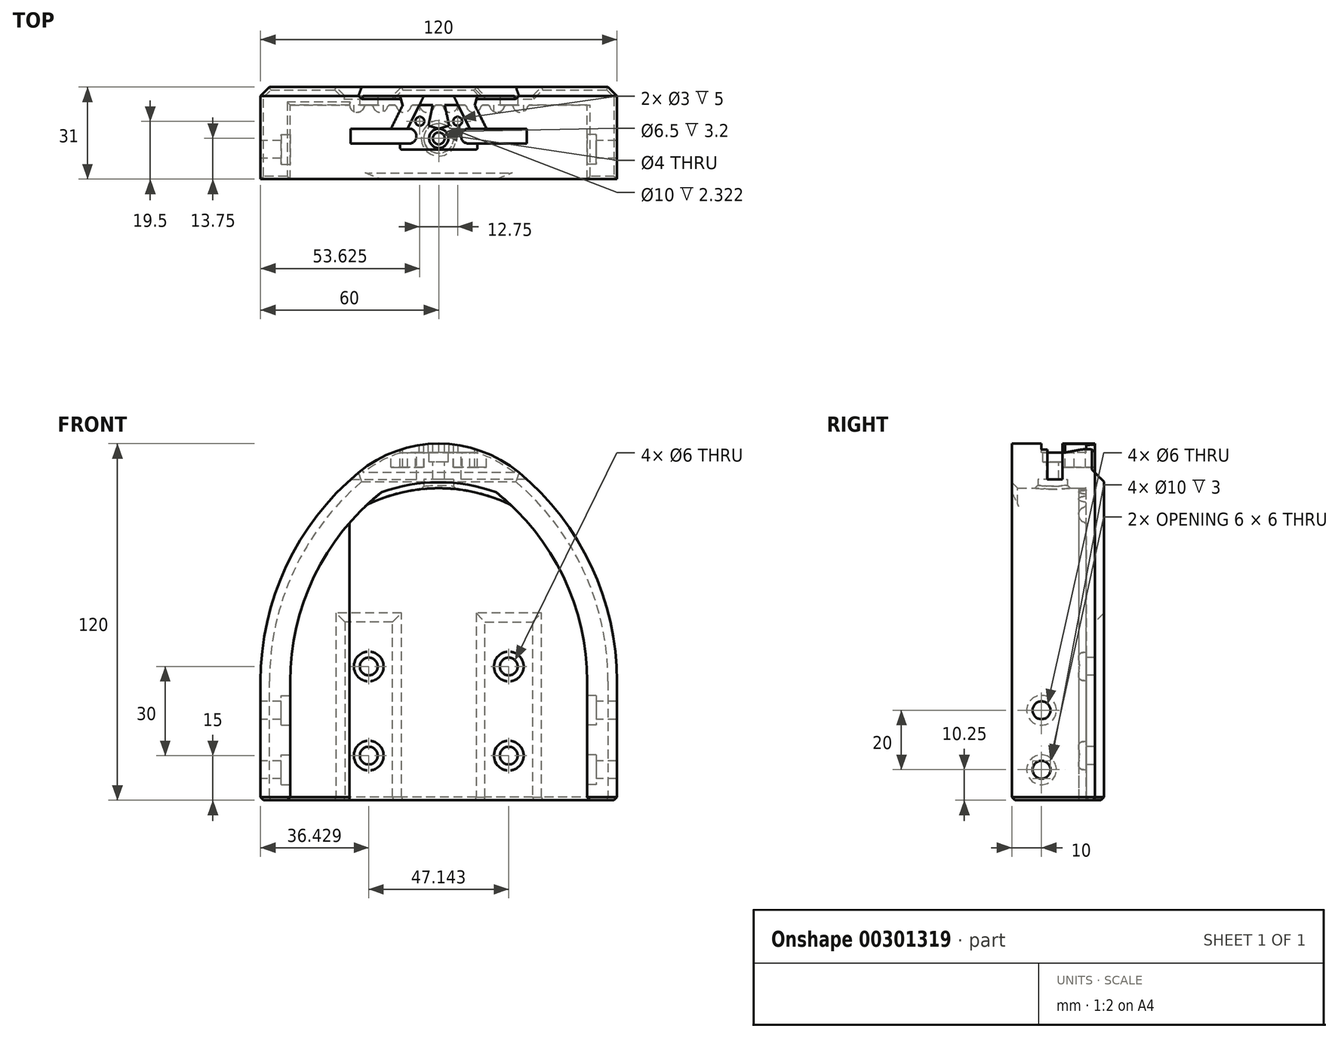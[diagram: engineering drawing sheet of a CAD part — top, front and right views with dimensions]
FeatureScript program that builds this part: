
annotation { "Feature Type Name" : "Feature", "Feature Type Description" : "" }
export const myFeature = defineFeature(function(context is Context, id is Id, definition is map)
    precondition{}
    {
        {
            assignVariable(context, id + "F0", {"name" : "LHeel", "anyValue" : 120 * mm});
        }
        {
            assignVariable(context, id + "F1", {"name" : "THeel", "anyValue" : 15 * mm});
        }
        {
            var Q0;
            Q0=qCreatedBy(makeId("Front.planeOp"),FACE);
            var sketch = newSketch(context, id + "F2", { "sketchPlane" : qUnion([Q0])});
            skArc(sketch, "E0", {"start": v(0, 120) * mm, "mid": v(-14.38, 117.48) * mm, "end": v(-27.05, 110.22) * mm});
            skArc(sketch, "E1", {"start": v(-27.05, 110.22) * mm, "mid": v(-51.35, 78.78) * mm, "end": v(-60, 40) * mm});
            skArc(sketch, "E2.MirrorCS", {"start": v(0, 120) * mm, "mid": v(14.38, 117.48) * mm, "end": v(27.05, 110.22) * mm});
            skArc(sketch, "E3.MirrorCS", {"start": v(27.05, 110.22) * mm, "mid": v(51.35, 78.78) * mm, "end": v(60, 40) * mm});
            skLineSegment(sketch, "E4.top", {"start": v(-60, 0) * mm, "end": v(60, 0) * mm});
            skLineSegment(sketch, "E4.left", {"start": v(-60, 40) * mm, "end": v(-60, 0) * mm});
            skLineSegment(sketch, "E4.right", {"start": v(60, 40) * mm, "end": v(60, 0) * mm});
            skSolve(sketch);
        }
        {
            var Q0;
            Q0=makeQuery(id+"F2.imprint","IMPRINT",FACE,{"disambiguationData":[TD([[makeQuery(id+"F2.imprint","IMPRINT",EDGE,{"derivedFrom":sQuery(id+"F2.wireOp",EDGE,"E0")}),1.0]])]});
            var Q1;
            Q1=makeQuery(id+"F2.imprint","IMPRINT",FACE,{"disambiguationData":[TD([[makeQuery(id+"F2.imprint","IMPRINT",EDGE,{"derivedFrom":sQuery(id+"F2.wireOp",EDGE,"auNxbXKF-pK2V-sqXS-c08M-DIaJRCpJJF02")}),-1.0]])]});
            extrude(context, id + "F3", {"entities" : qUnion([Q0, Q1]), "depth" : 3 * mm});
        }
        {
            var Q0;
            Q0=makeQuery(id+"F3.opExtrude","CAP_FACE",FACE,{"disambiguationData":[OSD([sQuery(id+"F2.wireOp",EDGE,"E0"),sQuery(id+"F2.wireOp",EDGE,"E1"),sQuery(id+"F2.wireOp",EDGE,"auNxbXKF-pK2V-sqXS-c08M-DIaJRCpJJF02"),sQuery(id+"F2.wireOp",EDGE,"E2.MirrorCS"),sQuery(id+"F2.wireOp",EDGE,"E3.MirrorCS"),sQuery(id+"F2.wireOp",EDGE,"bd82aa62-3da5-4588-8fb8-dd676fb609a00.MirrorCS")])],"isStart":false});
            var sketch = newSketch(context, id + "F4", { "sketchPlane" : qUnion([Q0])});
            skArc(sketch, "E5", {"start": v(0, 120) * mm, "mid": v(-14.38, 117.48) * mm, "end": v(-27.05, 110.22) * mm});
            skLineSegment(sketch, "E6", {"start": v(-27.05, 110.22) * mm, "end": v(-27.05, 110.22) * mm});
            skLineSegment(sketch, "E7.MirrorCS", {"start": v(27.05, 110.22) * mm, "end": v(27.05, 110.22) * mm});
            skArc(sketch, "E8.MirrorCS", {"start": v(0, 120) * mm, "mid": v(14.38, 117.48) * mm, "end": v(27.05, 110.22) * mm});
            skArc(sketch, "E9", {"start": v(24.26, 99.36) * mm, "mid": v(0, 105) * mm, "end": v(-24.26, 99.36) * mm});
            skPoint(sketch, "E10", {"position": v(0, 105) * mm});
            skArc(sketch, "E11", {"start": v(60, 40) * mm, "mid": v(51.35, 78.78) * mm, "end": v(27.05, 110.22) * mm});
            skArc(sketch, "E12", {"start": v(-27.05, 110.22) * mm, "mid": v(-51.35, 78.78) * mm, "end": v(-60, 40) * mm});
            skArc(sketch, "E13", {"start": v(-24.26, 99.36) * mm, "mid": v(-43.29, 72.35) * mm, "end": v(-50, 40) * mm});
            skArc(sketch, "E14", {"start": v(50, 40) * mm, "mid": v(43.29, 72.35) * mm, "end": v(24.26, 99.36) * mm});
            skLineSegment(sketch, "E15", {"start": v(-60, 40) * mm, "end": v(-60, 0) * mm});
            skLineSegment(sketch, "E16", {"start": v(-60, 0) * mm, "end": v(-50, 0) * mm});
            skLineSegment(sketch, "E17", {"start": v(-50, 0) * mm, "end": v(-50, 40) * mm});
            skLineSegment(sketch, "E18", {"start": v(50, 40) * mm, "end": v(50, 0) * mm});
            skLineSegment(sketch, "E19", {"start": v(50, 0) * mm, "end": v(60, 0) * mm});
            skLineSegment(sketch, "E20", {"start": v(60, 0) * mm, "end": v(60, 40) * mm});
            skSolve(sketch);
        }
        {
            var Q0;
            Q0=qSketchRegion(id+"F4",true);
            extrude(context, id + "F5", {"entities" : qUnion([Q0]), "operationType" : NewBodyOperationType.ADD, "depth" : 25 * mm});
        }
        {
            var Q0;
            Q0=makeQuery(id+"F5.boolean.opBoolean","MERGE",FACE,{"derivedFrom":[makeQuery(id+"F3.opExtrude","SWEPT_FACE",FACE,{"disambiguationData":[OSD([sQuery(id+"F2.wireOp",EDGE,"E4.top")])]}),makeQuery(id+"F5.opExtrude","SWEPT_FACE",FACE,{"disambiguationData":[OSD([sQuery(id+"F4.wireOp",EDGE,"E16")])]}),makeQuery(id+"F5.opExtrude","SWEPT_FACE",FACE,{"disambiguationData":[OSD([sQuery(id+"F4.wireOp",EDGE,"E19")])]})]});
            var sketch = newSketch(context, id + "F6", { "sketchPlane" : qUnion([Q0])});
            skArc(sketch, "E21", {"start": v(-25, 3) * mm, "mid": v(-27.5, 5.5) * mm, "end": v(-30, 3) * mm});
            skLineSegment(sketch, "E22", {"start": v(-30, 3) * mm, "end": v(-25, 3) * mm});
            skArc(sketch, "E23.1.0.0", {"start": v(-17.14, 3) * mm, "mid": v(-19.64, 5.5) * mm, "end": v(-22.14, 3) * mm});
            skArc(sketch, "E23.2.0.0", {"start": v(-9.29, 3) * mm, "mid": v(-11.79, 5.5) * mm, "end": v(-14.29, 3) * mm});
            skArc(sketch, "E23.3.0.0", {"start": v(-1.43, 3) * mm, "mid": v(-3.93, 5.5) * mm, "end": v(-6.43, 3) * mm});
            skArc(sketch, "E23.4.0.0", {"start": v(6.43, 3) * mm, "mid": v(3.93, 5.5) * mm, "end": v(1.43, 3) * mm});
            skArc(sketch, "E23.5.0.0", {"start": v(14.29, 3) * mm, "mid": v(11.79, 5.5) * mm, "end": v(9.29, 3) * mm});
            skArc(sketch, "E23.6.0.0", {"start": v(22.14, 3) * mm, "mid": v(19.64, 5.5) * mm, "end": v(17.14, 3) * mm});
            skArc(sketch, "E23.7.0.0", {"start": v(30, 3) * mm, "mid": v(27.5, 5.5) * mm, "end": v(25, 3) * mm});
            skLineSegment(sketch, "E23.direction1", {"start": v(-30, 3) * mm, "end": v(-22.14, 3) * mm, "construction": true});
            skSolve(sketch);
        }
        {
            var Q0;
            Q0=qSketchRegion(id+"F6",true);
            var Q1;
            {var subQ0=sQuery(id+"F6.wireOp",EDGE,"E23.1.0.0");Q1=makeQuery(id+"F6.imprint","IMPRINT",FACE,{"disambiguationData":[TD([[makeQuery(id+"F6.imprint","IMPRINT",EDGE,{"derivedFrom":subQ0}),1.0]])]});}
            var Q2;
            {var subQ0=sQuery(id+"F6.wireOp",EDGE,"E23.2.0.0");Q2=makeQuery(id+"F6.imprint","IMPRINT",FACE,{"disambiguationData":[TD([[makeQuery(id+"F6.imprint","IMPRINT",EDGE,{"derivedFrom":subQ0}),1.0]])]});}
            var Q3;
            {var subQ0=sQuery(id+"F6.wireOp",EDGE,"E23.3.0.0");Q3=makeQuery(id+"F6.imprint","IMPRINT",FACE,{"disambiguationData":[TD([[makeQuery(id+"F6.imprint","IMPRINT",EDGE,{"derivedFrom":subQ0}),1.0]])]});}
            var Q4;
            {var subQ0=sQuery(id+"F6.wireOp",EDGE,"E23.4.0.0");Q4=makeQuery(id+"F6.imprint","IMPRINT",FACE,{"disambiguationData":[TD([[makeQuery(id+"F6.imprint","IMPRINT",EDGE,{"derivedFrom":subQ0}),1.0]])]});}
            var Q5;
            {var subQ0=sQuery(id+"F6.wireOp",EDGE,"E23.5.0.0");Q5=makeQuery(id+"F6.imprint","IMPRINT",FACE,{"disambiguationData":[TD([[makeQuery(id+"F6.imprint","IMPRINT",EDGE,{"derivedFrom":subQ0}),1.0]])]});}
            var Q6;
            {var subQ0=sQuery(id+"F6.wireOp",EDGE,"E23.6.0.0");Q6=makeQuery(id+"F6.imprint","IMPRINT",FACE,{"disambiguationData":[TD([[makeQuery(id+"F6.imprint","IMPRINT",EDGE,{"derivedFrom":subQ0}),1.0]])]});}
            var Q7;
            {var subQ0=sQuery(id+"F6.wireOp",EDGE,"E23.7.0.0");Q7=makeQuery(id+"F6.imprint","IMPRINT",FACE,{"disambiguationData":[TD([[makeQuery(id+"F6.imprint","IMPRINT",EDGE,{"derivedFrom":subQ0}),1.0]])]});}
            var Q8;
            {var subQ0=sQuery(id+"F6.wireOp",EDGE,"E23.8.0.0");Q8=makeQuery(id+"F6.imprint","IMPRINT",FACE,{"disambiguationData":[TD([[makeQuery(id+"F6.imprint","IMPRINT",EDGE,{"derivedFrom":subQ0}),1.0]])]});}
            var Q9;
            {var subQ0=sQuery(id+"F6.wireOp",EDGE,"E23.9.0.0");Q9=makeQuery(id+"F6.imprint","IMPRINT",FACE,{"disambiguationData":[TD([[makeQuery(id+"F6.imprint","IMPRINT",EDGE,{"derivedFrom":subQ0}),1.0]])]});}
            extrude(context, id + "F7", {"entities" : qUnion([Q0, Q1, Q2, Q3, Q4, Q5, Q6, Q7, Q8, Q9]), "operationType" : NewBodyOperationType.ADD, "endBound" : BoundingType.UP_TO_NEXT, "oppositeDirection" : true, "depth" : 25 * mm});
        }
        {
            var Q0;
            {var subQ0=sQuery(id+"F6.wireOp",EDGE,"E22");var subQ1=sQuery(id+"F6.wireOp",EDGE,"E21");var subQ2=sQuery(id+"F2.wireOp",EDGE,"bd82aa62-3da5-4588-8fb8-dd676fb609a00.MirrorCS");var subQ3=sQuery(id+"F2.wireOp",EDGE,"auNxbXKF-pK2V-sqXS-c08M-DIaJRCpJJF02");Q0=makeQuery(id+"F7.opExtrude","SWEPT_EDGE",EDGE,{"disambiguationData":[OSD([subQ3,subQ2,subQ1,subQ0]),TDD([makeQuery(id+"F6.imprint","INTERSECT",VERTEX,{"disambiguationData":[OD(0.0)],"derivedFrom":[makeQuery(id+"F3.opExtrude","CAP_EDGE",EDGE,{"disambiguationData":[OSD([subQ3,subQ2])],"isStart":false}),subQ1,subQ0]})])]});}
            var Q1;
            {var subQ0=sQuery(id+"F6.wireOp",EDGE,"E23.1.0.0");var subQ1=sQuery(id+"F2.wireOp",EDGE,"bd82aa62-3da5-4588-8fb8-dd676fb609a00.MirrorCS");var subQ2=sQuery(id+"F2.wireOp",EDGE,"auNxbXKF-pK2V-sqXS-c08M-DIaJRCpJJF02");Q1=makeQuery(id+"F7.opExtrude","SWEPT_EDGE",EDGE,{"disambiguationData":[OSD([subQ2,subQ1,subQ0]),TDD([makeQuery(id+"F6.imprint","INTERSECT",VERTEX,{"disambiguationData":[OD(0.0)],"derivedFrom":[makeQuery(id+"F3.opExtrude","CAP_EDGE",EDGE,{"disambiguationData":[OSD([subQ2,subQ1])],"isStart":false}),subQ0]})])]});}
            var Q2;
            {var subQ0=sQuery(id+"F6.wireOp",EDGE,"E23.2.0.0");var subQ1=sQuery(id+"F2.wireOp",EDGE,"bd82aa62-3da5-4588-8fb8-dd676fb609a00.MirrorCS");var subQ2=sQuery(id+"F2.wireOp",EDGE,"auNxbXKF-pK2V-sqXS-c08M-DIaJRCpJJF02");Q2=makeQuery(id+"F7.opExtrude","SWEPT_EDGE",EDGE,{"disambiguationData":[OSD([subQ2,subQ1,subQ0]),TDD([makeQuery(id+"F6.imprint","INTERSECT",VERTEX,{"disambiguationData":[OD(0.0)],"derivedFrom":[makeQuery(id+"F3.opExtrude","CAP_EDGE",EDGE,{"disambiguationData":[OSD([subQ2,subQ1])],"isStart":false}),subQ0]})])]});}
            var Q3;
            {var subQ0=sQuery(id+"F6.wireOp",EDGE,"E23.3.0.0");var subQ1=sQuery(id+"F2.wireOp",EDGE,"bd82aa62-3da5-4588-8fb8-dd676fb609a00.MirrorCS");var subQ2=sQuery(id+"F2.wireOp",EDGE,"auNxbXKF-pK2V-sqXS-c08M-DIaJRCpJJF02");Q3=makeQuery(id+"F7.opExtrude","SWEPT_EDGE",EDGE,{"disambiguationData":[OSD([subQ2,subQ1,subQ0]),TDD([makeQuery(id+"F6.imprint","INTERSECT",VERTEX,{"disambiguationData":[OD(0.0)],"derivedFrom":[makeQuery(id+"F3.opExtrude","CAP_EDGE",EDGE,{"disambiguationData":[OSD([subQ2,subQ1])],"isStart":false}),subQ0]})])]});}
            var Q4;
            {var subQ0=sQuery(id+"F6.wireOp",EDGE,"E23.4.0.0");var subQ1=sQuery(id+"F2.wireOp",EDGE,"bd82aa62-3da5-4588-8fb8-dd676fb609a00.MirrorCS");var subQ2=sQuery(id+"F2.wireOp",EDGE,"auNxbXKF-pK2V-sqXS-c08M-DIaJRCpJJF02");Q4=makeQuery(id+"F7.opExtrude","SWEPT_EDGE",EDGE,{"disambiguationData":[OSD([subQ2,subQ1,subQ0]),TDD([makeQuery(id+"F6.imprint","INTERSECT",VERTEX,{"disambiguationData":[OD(0.0)],"derivedFrom":[makeQuery(id+"F3.opExtrude","CAP_EDGE",EDGE,{"disambiguationData":[OSD([subQ2,subQ1])],"isStart":false}),subQ0]})])]});}
            var Q5;
            {var subQ0=sQuery(id+"F6.wireOp",EDGE,"E23.5.0.0");var subQ1=sQuery(id+"F2.wireOp",EDGE,"bd82aa62-3da5-4588-8fb8-dd676fb609a00.MirrorCS");var subQ2=sQuery(id+"F2.wireOp",EDGE,"auNxbXKF-pK2V-sqXS-c08M-DIaJRCpJJF02");Q5=makeQuery(id+"F7.opExtrude","SWEPT_EDGE",EDGE,{"disambiguationData":[OSD([subQ2,subQ1,subQ0]),TDD([makeQuery(id+"F6.imprint","INTERSECT",VERTEX,{"disambiguationData":[OD(0.0)],"derivedFrom":[makeQuery(id+"F3.opExtrude","CAP_EDGE",EDGE,{"disambiguationData":[OSD([subQ2,subQ1])],"isStart":false}),subQ0]})])]});}
            var Q6;
            {var subQ0=sQuery(id+"F6.wireOp",EDGE,"E23.6.0.0");var subQ1=sQuery(id+"F2.wireOp",EDGE,"bd82aa62-3da5-4588-8fb8-dd676fb609a00.MirrorCS");var subQ2=sQuery(id+"F2.wireOp",EDGE,"auNxbXKF-pK2V-sqXS-c08M-DIaJRCpJJF02");Q6=makeQuery(id+"F7.opExtrude","SWEPT_EDGE",EDGE,{"disambiguationData":[OSD([subQ2,subQ1,subQ0]),TDD([makeQuery(id+"F6.imprint","INTERSECT",VERTEX,{"disambiguationData":[OD(0.0)],"derivedFrom":[makeQuery(id+"F3.opExtrude","CAP_EDGE",EDGE,{"disambiguationData":[OSD([subQ2,subQ1])],"isStart":false}),subQ0]})])]});}
            var Q7;
            {var subQ0=sQuery(id+"F6.wireOp",EDGE,"E23.7.0.0");var subQ1=sQuery(id+"F2.wireOp",EDGE,"bd82aa62-3da5-4588-8fb8-dd676fb609a00.MirrorCS");var subQ2=sQuery(id+"F2.wireOp",EDGE,"auNxbXKF-pK2V-sqXS-c08M-DIaJRCpJJF02");Q7=makeQuery(id+"F7.opExtrude","SWEPT_EDGE",EDGE,{"disambiguationData":[OSD([subQ2,subQ1,subQ0]),TDD([makeQuery(id+"F6.imprint","INTERSECT",VERTEX,{"disambiguationData":[OD(0.0)],"derivedFrom":[makeQuery(id+"F3.opExtrude","CAP_EDGE",EDGE,{"disambiguationData":[OSD([subQ2,subQ1])],"isStart":false}),subQ0]})])]});}
            var Q8;
            {var subQ0=sQuery(id+"F6.wireOp",EDGE,"E23.8.0.0");var subQ1=sQuery(id+"F2.wireOp",EDGE,"bd82aa62-3da5-4588-8fb8-dd676fb609a00.MirrorCS");var subQ2=sQuery(id+"F2.wireOp",EDGE,"auNxbXKF-pK2V-sqXS-c08M-DIaJRCpJJF02");Q8=makeQuery(id+"F7.opExtrude","SWEPT_EDGE",EDGE,{"disambiguationData":[OSD([subQ2,subQ1,subQ0]),TDD([makeQuery(id+"F6.imprint","INTERSECT",VERTEX,{"disambiguationData":[OD(0.0)],"derivedFrom":[makeQuery(id+"F3.opExtrude","CAP_EDGE",EDGE,{"disambiguationData":[OSD([subQ2,subQ1])],"isStart":false}),subQ0]})])]});}
            var Q9;
            {var subQ0=sQuery(id+"F6.wireOp",EDGE,"E23.9.0.0");var subQ1=sQuery(id+"F2.wireOp",EDGE,"bd82aa62-3da5-4588-8fb8-dd676fb609a00.MirrorCS");var subQ2=sQuery(id+"F2.wireOp",EDGE,"auNxbXKF-pK2V-sqXS-c08M-DIaJRCpJJF02");Q9=makeQuery(id+"F7.opExtrude","SWEPT_EDGE",EDGE,{"disambiguationData":[OSD([subQ2,subQ1,subQ0]),TDD([makeQuery(id+"F6.imprint","INTERSECT",VERTEX,{"disambiguationData":[OD(0.0)],"derivedFrom":[makeQuery(id+"F3.opExtrude","CAP_EDGE",EDGE,{"disambiguationData":[OSD([subQ2,subQ1])],"isStart":false}),subQ0]})])]});}
            var Q10;
            {var subQ0=sQuery(id+"F6.wireOp",EDGE,"E23.9.0.0");var subQ1=sQuery(id+"F2.wireOp",EDGE,"bd82aa62-3da5-4588-8fb8-dd676fb609a00.MirrorCS");var subQ2=sQuery(id+"F2.wireOp",EDGE,"auNxbXKF-pK2V-sqXS-c08M-DIaJRCpJJF02");Q10=makeQuery(id+"F7.opExtrude","SWEPT_EDGE",EDGE,{"disambiguationData":[OSD([subQ2,subQ1,subQ0]),TDD([makeQuery(id+"F6.imprint","INTERSECT",VERTEX,{"disambiguationData":[OD(1.0)],"derivedFrom":[makeQuery(id+"F3.opExtrude","CAP_EDGE",EDGE,{"disambiguationData":[OSD([subQ2,subQ1])],"isStart":false}),subQ0]})])]});}
            var Q11;
            {var subQ0=sQuery(id+"F6.wireOp",EDGE,"E23.8.0.0");var subQ1=sQuery(id+"F2.wireOp",EDGE,"bd82aa62-3da5-4588-8fb8-dd676fb609a00.MirrorCS");var subQ2=sQuery(id+"F2.wireOp",EDGE,"auNxbXKF-pK2V-sqXS-c08M-DIaJRCpJJF02");Q11=makeQuery(id+"F7.opExtrude","SWEPT_EDGE",EDGE,{"disambiguationData":[OSD([subQ2,subQ1,subQ0]),TDD([makeQuery(id+"F6.imprint","INTERSECT",VERTEX,{"disambiguationData":[OD(1.0)],"derivedFrom":[makeQuery(id+"F3.opExtrude","CAP_EDGE",EDGE,{"disambiguationData":[OSD([subQ2,subQ1])],"isStart":false}),subQ0]})])]});}
            var Q12;
            {var subQ0=sQuery(id+"F6.wireOp",EDGE,"E23.7.0.0");var subQ1=sQuery(id+"F2.wireOp",EDGE,"bd82aa62-3da5-4588-8fb8-dd676fb609a00.MirrorCS");var subQ2=sQuery(id+"F2.wireOp",EDGE,"auNxbXKF-pK2V-sqXS-c08M-DIaJRCpJJF02");Q12=makeQuery(id+"F7.opExtrude","SWEPT_EDGE",EDGE,{"disambiguationData":[OSD([subQ2,subQ1,subQ0]),TDD([makeQuery(id+"F6.imprint","INTERSECT",VERTEX,{"disambiguationData":[OD(1.0)],"derivedFrom":[makeQuery(id+"F3.opExtrude","CAP_EDGE",EDGE,{"disambiguationData":[OSD([subQ2,subQ1])],"isStart":false}),subQ0]})])]});}
            var Q13;
            {var subQ0=sQuery(id+"F6.wireOp",EDGE,"E23.6.0.0");var subQ1=sQuery(id+"F2.wireOp",EDGE,"bd82aa62-3da5-4588-8fb8-dd676fb609a00.MirrorCS");var subQ2=sQuery(id+"F2.wireOp",EDGE,"auNxbXKF-pK2V-sqXS-c08M-DIaJRCpJJF02");Q13=makeQuery(id+"F7.opExtrude","SWEPT_EDGE",EDGE,{"disambiguationData":[OSD([subQ2,subQ1,subQ0]),TDD([makeQuery(id+"F6.imprint","INTERSECT",VERTEX,{"disambiguationData":[OD(1.0)],"derivedFrom":[makeQuery(id+"F3.opExtrude","CAP_EDGE",EDGE,{"disambiguationData":[OSD([subQ2,subQ1])],"isStart":false}),subQ0]})])]});}
            var Q14;
            {var subQ0=sQuery(id+"F6.wireOp",EDGE,"E23.5.0.0");var subQ1=sQuery(id+"F2.wireOp",EDGE,"bd82aa62-3da5-4588-8fb8-dd676fb609a00.MirrorCS");var subQ2=sQuery(id+"F2.wireOp",EDGE,"auNxbXKF-pK2V-sqXS-c08M-DIaJRCpJJF02");Q14=makeQuery(id+"F7.opExtrude","SWEPT_EDGE",EDGE,{"disambiguationData":[OSD([subQ2,subQ1,subQ0]),TDD([makeQuery(id+"F6.imprint","INTERSECT",VERTEX,{"disambiguationData":[OD(1.0)],"derivedFrom":[makeQuery(id+"F3.opExtrude","CAP_EDGE",EDGE,{"disambiguationData":[OSD([subQ2,subQ1])],"isStart":false}),subQ0]})])]});}
            var Q15;
            {var subQ0=sQuery(id+"F6.wireOp",EDGE,"E23.4.0.0");var subQ1=sQuery(id+"F2.wireOp",EDGE,"bd82aa62-3da5-4588-8fb8-dd676fb609a00.MirrorCS");var subQ2=sQuery(id+"F2.wireOp",EDGE,"auNxbXKF-pK2V-sqXS-c08M-DIaJRCpJJF02");Q15=makeQuery(id+"F7.opExtrude","SWEPT_EDGE",EDGE,{"disambiguationData":[OSD([subQ2,subQ1,subQ0]),TDD([makeQuery(id+"F6.imprint","INTERSECT",VERTEX,{"disambiguationData":[OD(1.0)],"derivedFrom":[makeQuery(id+"F3.opExtrude","CAP_EDGE",EDGE,{"disambiguationData":[OSD([subQ2,subQ1])],"isStart":false}),subQ0]})])]});}
            var Q16;
            {var subQ0=sQuery(id+"F6.wireOp",EDGE,"E23.3.0.0");var subQ1=sQuery(id+"F2.wireOp",EDGE,"bd82aa62-3da5-4588-8fb8-dd676fb609a00.MirrorCS");var subQ2=sQuery(id+"F2.wireOp",EDGE,"auNxbXKF-pK2V-sqXS-c08M-DIaJRCpJJF02");Q16=makeQuery(id+"F7.opExtrude","SWEPT_EDGE",EDGE,{"disambiguationData":[OSD([subQ2,subQ1,subQ0]),TDD([makeQuery(id+"F6.imprint","INTERSECT",VERTEX,{"disambiguationData":[OD(1.0)],"derivedFrom":[makeQuery(id+"F3.opExtrude","CAP_EDGE",EDGE,{"disambiguationData":[OSD([subQ2,subQ1])],"isStart":false}),subQ0]})])]});}
            var Q17;
            {var subQ0=sQuery(id+"F6.wireOp",EDGE,"E23.2.0.0");var subQ1=sQuery(id+"F2.wireOp",EDGE,"bd82aa62-3da5-4588-8fb8-dd676fb609a00.MirrorCS");var subQ2=sQuery(id+"F2.wireOp",EDGE,"auNxbXKF-pK2V-sqXS-c08M-DIaJRCpJJF02");Q17=makeQuery(id+"F7.opExtrude","SWEPT_EDGE",EDGE,{"disambiguationData":[OSD([subQ2,subQ1,subQ0]),TDD([makeQuery(id+"F6.imprint","INTERSECT",VERTEX,{"disambiguationData":[OD(1.0)],"derivedFrom":[makeQuery(id+"F3.opExtrude","CAP_EDGE",EDGE,{"disambiguationData":[OSD([subQ2,subQ1])],"isStart":false}),subQ0]})])]});}
            var Q18;
            {var subQ0=sQuery(id+"F6.wireOp",EDGE,"E23.1.0.0");var subQ1=sQuery(id+"F2.wireOp",EDGE,"bd82aa62-3da5-4588-8fb8-dd676fb609a00.MirrorCS");var subQ2=sQuery(id+"F2.wireOp",EDGE,"auNxbXKF-pK2V-sqXS-c08M-DIaJRCpJJF02");Q18=makeQuery(id+"F7.opExtrude","SWEPT_EDGE",EDGE,{"disambiguationData":[OSD([subQ2,subQ1,subQ0]),TDD([makeQuery(id+"F6.imprint","INTERSECT",VERTEX,{"disambiguationData":[OD(1.0)],"derivedFrom":[makeQuery(id+"F3.opExtrude","CAP_EDGE",EDGE,{"disambiguationData":[OSD([subQ2,subQ1])],"isStart":false}),subQ0]})])]});}
            var Q19;
            {var subQ0=sQuery(id+"F6.wireOp",EDGE,"E22");var subQ1=sQuery(id+"F6.wireOp",EDGE,"E21");var subQ2=sQuery(id+"F2.wireOp",EDGE,"bd82aa62-3da5-4588-8fb8-dd676fb609a00.MirrorCS");var subQ3=sQuery(id+"F2.wireOp",EDGE,"auNxbXKF-pK2V-sqXS-c08M-DIaJRCpJJF02");Q19=makeQuery(id+"F7.opExtrude","SWEPT_EDGE",EDGE,{"disambiguationData":[OSD([subQ3,subQ2,subQ1,subQ0]),TDD([makeQuery(id+"F6.imprint","INTERSECT",VERTEX,{"disambiguationData":[OD(1.0)],"derivedFrom":[makeQuery(id+"F3.opExtrude","CAP_EDGE",EDGE,{"disambiguationData":[OSD([subQ3,subQ2])],"isStart":false}),subQ1,subQ0]})])]});}
            fillet(context, id + "F8", {"entities" : qUnion([Q0, Q1, Q2, Q3, Q4, Q5, Q6, Q7, Q8, Q9, Q10, Q11, Q12, Q13, Q14, Q15, Q16, Q17, Q18, Q19]), "radius" : 1 * mm, "tangentPropagation" : true, "allowEdgeOverflow" : false});
        }
        {
            var Q0;
            Q0=qCreatedBy(makeId("Top.planeOp"),FACE);
            cPlane(context, id + "F9", {"entities" : qUnion([Q0]), "cplaneType" : CPlaneType.OFFSET, "offset" : getVariable(context, 'LHeel'), "width" : 150 * mm, "height" : 150 * mm});
        }
        {
            var Q0;
            Q0=qCreatedBy(id+"F9.planeOp",FACE);
            var sketch = newSketch(context, id + "F10", { "sketchPlane" : qUnion([Q0])});
            skLineSegment(sketch, "E24", {"start": v(35, -11) * mm, "end": v(10, -11) * mm});
            skLineSegment(sketch, "E25", {"start": v(10, -16) * mm, "end": v(35, -16) * mm});
            skLineSegment(sketch, "E26", {"start": v(35, -16) * mm, "end": v(35, -11) * mm});
            skArc(sketch, "E27", {"start": v(10, -11) * mm, "mid": v(7.5, -13.5) * mm, "end": v(10, -16) * mm});
            skLineSegment(sketch, "E28.MirrorCS", {"start": v(-35, -11) * mm, "end": v(-10, -11) * mm});
            skLineSegment(sketch, "E29.MirrorCS", {"start": v(-35, -16) * mm, "end": v(-35, -11) * mm});
            skLineSegment(sketch, "E30.MirrorCS", {"start": v(-10, -16) * mm, "end": v(-35, -16) * mm});
            skArc(sketch, "E31.MirrorCS", {"start": v(-10, -11) * mm, "mid": v(-7.5, -13.5) * mm, "end": v(-10, -16) * mm});
            skSolve(sketch);
        }
        {
            var Q0;
            Q0=qSketchRegion(id+"F10",true);
            extrude(context, id + "F11", {"entities" : qUnion([Q0]), "operationType" : NewBodyOperationType.REMOVE, "oppositeDirection" : true, "depth" : 12 * mm});
        }
        {
            var Q0;
            Q0=qCreatedBy(id+"F9.planeOp",FACE);
            var sketch = newSketch(context, id + "F12", { "sketchPlane" : qUnion([Q0])});
            skLineSegment(sketch, "E32", {"start": v(-5, 0) * mm, "end": v(-10.5, -11) * mm});
            skLineSegment(sketch, "E33", {"start": v(-10.5, -11) * mm, "end": v(-16.1, -11) * mm});
            skLineSegment(sketch, "E34", {"start": v(-16.1, -11) * mm, "end": v(-12.16, -3.14) * mm});
            skLineSegment(sketch, "E35", {"start": v(-12.16, -3.14) * mm, "end": v(-13, 0) * mm});
            skLineSegment(sketch, "E36", {"start": v(-13, 0) * mm, "end": v(-5, 0) * mm});
            skLineSegment(sketch, "E37.MirrorCS", {"start": v(12.16, -3.14) * mm, "end": v(13, 0) * mm});
            skLineSegment(sketch, "E38.MirrorCS", {"start": v(13, 0) * mm, "end": v(5, 0) * mm});
            skLineSegment(sketch, "E39.MirrorCS", {"start": v(10.5, -11) * mm, "end": v(16.1, -11) * mm});
            skLineSegment(sketch, "E40.MirrorCS", {"start": v(16.1, -11) * mm, "end": v(12.16, -3.14) * mm});
            skLineSegment(sketch, "E41.MirrorCS", {"start": v(5, 0) * mm, "end": v(10.5, -11) * mm});
            skSolve(sketch);
        }
        {
            var Q0;
            Q0=qSketchRegion(id+"F12",true);
            extrude(context, id + "F13", {"entities" : qUnion([Q0]), "operationType" : NewBodyOperationType.REMOVE, "oppositeDirection" : true, "depth" : 8 * mm});
        }
        {
            var Q0;
            Q0=qCreatedBy(id+"F9.planeOp",FACE);
            var sketch = newSketch(context, id + "F14", { "sketchPlane" : qUnion([Q0])});
            skLineSegment(sketch, "E42", {"start": v(-6.5, -3) * mm, "end": v(-2, -3) * mm});
            skLineSegment(sketch, "E43", {"start": v(-2, -3) * mm, "end": v(-3.5, -10) * mm});
            skLineSegment(sketch, "E44", {"start": v(-3.5, -10) * mm, "end": v(0, -11) * mm});
            skLineSegment(sketch, "E45", {"start": v(-6.5, -3) * mm, "end": v(-10.5, -11) * mm});
            skLineSegment(sketch, "E46", {"start": v(-13, -16) * mm, "end": v(-13, -18) * mm});
            skLineSegment(sketch, "E47", {"start": v(-13, -18) * mm, "end": v(0, -18) * mm});
            skLineSegment(sketch, "E48", {"start": v(-13, -16) * mm, "end": v(-10, -16) * mm});
            skLineSegment(sketch, "E49.MirrorCS", {"start": v(6.5, -3) * mm, "end": v(2, -3) * mm});
            skLineSegment(sketch, "E50.MirrorCS", {"start": v(6.5, -3) * mm, "end": v(10.5, -11) * mm});
            skLineSegment(sketch, "E51.MirrorCS", {"start": v(3.5, -10) * mm, "end": v(0, -11) * mm});
            skLineSegment(sketch, "E52.MirrorCS", {"start": v(2, -3) * mm, "end": v(3.5, -10) * mm});
            skLineSegment(sketch, "E53.MirrorCS", {"start": v(13, -16) * mm, "end": v(13, -18) * mm});
            skLineSegment(sketch, "E54.MirrorCS", {"start": v(13, -18) * mm, "end": v(0, -18) * mm});
            skLineSegment(sketch, "E55.MirrorCS", {"start": v(13, -16) * mm, "end": v(10, -16) * mm});
            skLineSegment(sketch, "E56", {"start": v(-10.5, -11) * mm, "end": v(-10, -11) * mm});
            skArc(sketch, "E57", {"start": v(-10, -16) * mm, "mid": v(-7.5, -13.5) * mm, "end": v(-10, -11) * mm});
            skLineSegment(sketch, "E58.MirrorCS", {"start": v(10.5, -11) * mm, "end": v(10, -11) * mm});
            skArc(sketch, "E59.MirrorCS", {"start": v(10, -16) * mm, "mid": v(7.5, -13.5) * mm, "end": v(10, -11) * mm});
            skSolve(sketch);
        }
        {
            var Q0;
            Q0=qSketchRegion(id+"F14",true);
            extrude(context, id + "F15", {"entities" : qUnion([Q0]), "operationType" : NewBodyOperationType.REMOVE, "oppositeDirection" : true, "depth" : 3 * mm});
        }
        {
            var Q0;
            Q0=makeQuery(id+"F15.boolean.opBoolean","COPY",EDGE,{"derivedFrom":makeQuery(id+"F15.opExtrude","SWEPT_EDGE",EDGE,{"disambiguationData":[OSD([sQuery(id+"F14.wireOp",EDGE,"E53.MirrorCS"),sQuery(id+"F14.wireOp",EDGE,"E54.MirrorCS")])]})});
            var Q1;
            Q1=makeQuery(id+"F15.boolean.opBoolean","COPY",EDGE,{"derivedFrom":makeQuery(id+"F15.opExtrude","SWEPT_EDGE",EDGE,{"disambiguationData":[OSD([sQuery(id+"F14.wireOp",EDGE,"E46"),sQuery(id+"F14.wireOp",EDGE,"E47")])]})});
            fillet(context, id + "F16", {"entities" : qUnion([Q0, Q1]), "radius" : .5 * mm, "tangentPropagation" : true, "allowEdgeOverflow" : false});
        }
        {
            var Q0;
            Q0=makeQuery(id+"F15.boolean.opBoolean","COPY",FACE,{"derivedFrom":makeQuery(id+"F15.opExtrude","CAP_FACE",FACE,{"disambiguationData":[OSD([sQuery(id+"F14.wireOp",EDGE,"E42"),sQuery(id+"F14.wireOp",EDGE,"E43"),sQuery(id+"F14.wireOp",EDGE,"E44"),sQuery(id+"F14.wireOp",EDGE,"E45"),sQuery(id+"F14.wireOp",EDGE,"E46"),sQuery(id+"F14.wireOp",EDGE,"E47"),sQuery(id+"F14.wireOp",EDGE,"E48"),sQuery(id+"F14.wireOp",EDGE,"E49.MirrorCS"),sQuery(id+"F14.wireOp",EDGE,"E50.MirrorCS"),sQuery(id+"F14.wireOp",EDGE,"E51.MirrorCS"),sQuery(id+"F14.wireOp",EDGE,"E52.MirrorCS"),sQuery(id+"F14.wireOp",EDGE,"E53.MirrorCS"),sQuery(id+"F14.wireOp",EDGE,"E54.MirrorCS"),sQuery(id+"F14.wireOp",EDGE,"E55.MirrorCS"),sQuery(id+"F14.wireOp",EDGE,"E56"),sQuery(id+"F14.wireOp",EDGE,"E57"),sQuery(id+"F14.wireOp",EDGE,"E58.MirrorCS"),sQuery(id+"F14.wireOp",EDGE,"E59.MirrorCS")])],"isStart":false})});
            var sketch = newSketch(context, id + "F17", { "sketchPlane" : qUnion([Q0])});
            skCircle(sketch, "E60", {"center": v(0, -14.25) * mm, "radius": 3.25 * mm});
            skSolve(sketch);
        }
        {
            var Q0;
            Q0=qSketchRegion(id+"F17",true);
            extrude(context, id + "F18", {"entities" : qUnion([Q0]), "operationType" : NewBodyOperationType.REMOVE, "oppositeDirection" : true, "depth" : 3.2 * mm});
        }
        {
            var Q0;
            Q0=makeQuery(id+"F15.boolean.opBoolean","COPY",FACE,{"derivedFrom":makeQuery(id+"F15.opExtrude","CAP_FACE",FACE,{"disambiguationData":[OSD([sQuery(id+"F14.wireOp",EDGE,"E42"),sQuery(id+"F14.wireOp",EDGE,"E43"),sQuery(id+"F14.wireOp",EDGE,"E44"),sQuery(id+"F14.wireOp",EDGE,"E45"),sQuery(id+"F14.wireOp",EDGE,"E46"),sQuery(id+"F14.wireOp",EDGE,"E47"),sQuery(id+"F14.wireOp",EDGE,"E48"),sQuery(id+"F14.wireOp",EDGE,"E49.MirrorCS"),sQuery(id+"F14.wireOp",EDGE,"E50.MirrorCS"),sQuery(id+"F14.wireOp",EDGE,"E51.MirrorCS"),sQuery(id+"F14.wireOp",EDGE,"E52.MirrorCS"),sQuery(id+"F14.wireOp",EDGE,"E53.MirrorCS"),sQuery(id+"F14.wireOp",EDGE,"E54.MirrorCS"),sQuery(id+"F14.wireOp",EDGE,"E55.MirrorCS"),sQuery(id+"F14.wireOp",EDGE,"E56"),sQuery(id+"F14.wireOp",EDGE,"E57"),sQuery(id+"F14.wireOp",EDGE,"E58.MirrorCS"),sQuery(id+"F14.wireOp",EDGE,"E59.MirrorCS")])],"isStart":false})});
            var sketch = newSketch(context, id + "F19", { "sketchPlane" : qUnion([Q0])});
            skCircle(sketch, "E61", {"center": v(6.38, -8.5) * mm, "radius": 1.5 * mm});
            skCircle(sketch, "E62.MirrorC", {"center": v(-6.38, -8.5) * mm, "radius": 1.5 * mm});
            skSolve(sketch);
        }
        {
            var Q0;
            Q0=qSketchRegion(id+"F19",true);
            extrude(context, id + "F20", {"entities" : qUnion([Q0]), "operationType" : NewBodyOperationType.REMOVE, "oppositeDirection" : true, "depth" : 5 * mm});
        }
        {
            var Q0;
            Q0=makeQuery(id+"F15.boolean.opBoolean","COPY",FACE,{"derivedFrom":makeQuery(id+"F15.opExtrude","CAP_FACE",FACE,{"disambiguationData":[OSD([sQuery(id+"F14.wireOp",EDGE,"E42"),sQuery(id+"F14.wireOp",EDGE,"E43"),sQuery(id+"F14.wireOp",EDGE,"E44"),sQuery(id+"F14.wireOp",EDGE,"E45"),sQuery(id+"F14.wireOp",EDGE,"E46"),sQuery(id+"F14.wireOp",EDGE,"E47"),sQuery(id+"F14.wireOp",EDGE,"E48"),sQuery(id+"F14.wireOp",EDGE,"E49.MirrorCS"),sQuery(id+"F14.wireOp",EDGE,"E50.MirrorCS"),sQuery(id+"F14.wireOp",EDGE,"E51.MirrorCS"),sQuery(id+"F14.wireOp",EDGE,"E52.MirrorCS"),sQuery(id+"F14.wireOp",EDGE,"E53.MirrorCS"),sQuery(id+"F14.wireOp",EDGE,"E54.MirrorCS"),sQuery(id+"F14.wireOp",EDGE,"E55.MirrorCS"),sQuery(id+"F14.wireOp",EDGE,"E56"),sQuery(id+"F14.wireOp",EDGE,"E57"),sQuery(id+"F14.wireOp",EDGE,"E58.MirrorCS"),sQuery(id+"F14.wireOp",EDGE,"E59.MirrorCS")])],"isStart":false})});
            var sketch = newSketch(context, id + "F21", { "sketchPlane" : qUnion([Q0])});
            skCircle(sketch, "E63", {"center": v(0, -14.25) * mm, "radius": 2 * mm});
            skSolve(sketch);
        }
        {
            var Q0;
            Q0=qSketchRegion(id+"F21",true);
            extrude(context, id + "F22", {"entities" : qUnion([Q0]), "operationType" : NewBodyOperationType.REMOVE, "oppositeDirection" : true, "depth" : 25 * mm});
        }
        {
            var Q0;
            Q0=qCreatedBy(makeId("Top.planeOp"),FACE);
            cPlane(context, id + "F23", {"entities" : qUnion([Q0]), "cplaneType" : CPlaneType.OFFSET, "offset" : getVariable(context, 'LHeel') - getVariable(context, 'THeel'), "width" : 150 * mm, "height" : 150 * mm});
        }
        {
            var Q0;
            Q0=qCreatedBy(id+"F23.planeOp",FACE);
            var sketch = newSketch(context, id + "F24", { "sketchPlane" : qUnion([Q0])});
            skCircle(sketch, "E64", {"center": v(0, -14.25) * mm, "radius": 2 * mm});
            skCircle(sketch, "E65", {"center": v(0, -14.25) * mm, "radius": 5 * mm});
            skSolve(sketch);
        }
        {
            var Q0;
            Q0=qSketchRegion(id+"F24",true);
            extrude(context, id + "F25", {"entities" : qUnion([Q0]), "operationType" : NewBodyOperationType.REMOVE, "depth" : 3 * mm, "hasSecondDirection" : true, "secondDirectionOppositeDirection" : true, "secondDirectionDepth" : 25 * mm});
        }
        {
            var Q0;
            {var subQ0=sQuery(id+"F6.wireOp",EDGE,"E23.6.0.0");var subQ1=sQuery(id+"F2.wireOp",EDGE,"bd82aa62-3da5-4588-8fb8-dd676fb609a00.MirrorCS");var subQ2=sQuery(id+"F2.wireOp",EDGE,"auNxbXKF-pK2V-sqXS-c08M-DIaJRCpJJF02");var subQ3=makeQuery(id+"F7.opExtrude","CAP_FACE",FACE,{"disambiguationData":[OSD([subQ2,subQ1,subQ0])],"isStart":true});var subQ4=makeQuery(id+"F7.opExtrude","CAP_FACE",FACE,{"disambiguationData":[OSD([subQ2,subQ1,sQuery(id+"F6.wireOp",EDGE,"E23.4.0.0")])],"isStart":true});var subQ5=makeQuery(id+"F7.opExtrude","CAP_FACE",FACE,{"disambiguationData":[OSD([subQ2,subQ1,sQuery(id+"F6.wireOp",EDGE,"E23.3.0.0")])],"isStart":true});var subQ6=makeQuery(id+"F3.opExtrude","SWEPT_FACE",FACE,{"disambiguationData":[OSD([subQ2,subQ1])]});var subQ7=makeQuery(id+"F7.opExtrude","CAP_FACE",FACE,{"disambiguationData":[OSD([subQ2,subQ1,sQuery(id+"F6.wireOp",EDGE,"E23.2.0.0")])],"isStart":true});var subQ8=makeQuery(id+"F5.opExtrude","SWEPT_FACE",FACE,{"disambiguationData":[OSD([sQuery(id+"F4.wireOp",EDGE,"FZn0JHBI-A9Gq-jUhd-VDxp-ANsdCAXQZEyL"),sQuery(id+"F4.wireOp",EDGE,"94862bb9-d334-4f4f-86bf-2b5ff63ee9990.MirrorCS")])]});var subQ9=sQuery(id+"F6.wireOp",EDGE,"E23.7.0.0");var subQ10=makeQuery(id+"F7.opExtrude","SWEPT_FACE",FACE,{"disambiguationData":[OSD([subQ9])]});var subQ11=makeQuery(id+"F7.opExtrude","CAP_FACE",FACE,{"disambiguationData":[OSD([subQ2,subQ1,sQuery(id+"F6.wireOp",EDGE,"E23.1.0.0")])],"isStart":true});var subQ12=makeQuery(id+"F7.opExtrude","CAP_FACE",FACE,{"disambiguationData":[OSD([subQ2,subQ1,sQuery(id+"F6.wireOp",EDGE,"E23.5.0.0")])],"isStart":true});var subQ13=makeQuery(id+"F7.opExtrude","CAP_FACE",FACE,{"disambiguationData":[OSD([sQuery(id+"F6.wireOp",EDGE,"E21"),sQuery(id+"F6.wireOp",EDGE,"E22")])],"isStart":true});var subQ14=makeQuery(id+"F7.opExtrude","CAP_FACE",FACE,{"disambiguationData":[OSD([subQ2,subQ1,subQ9])],"isStart":true});var subQ15=sQuery(id+"F6.wireOp",EDGE,"E23.8.0.0");var subQ16=makeQuery(id+"F7.opExtrude","SWEPT_FACE",FACE,{"disambiguationData":[OSD([subQ15])]});var subQ17=makeQuery(id+"F7.opExtrude","CAP_FACE",FACE,{"disambiguationData":[OSD([subQ2,subQ1,subQ15])],"isStart":true});var subQ18=sQuery(id+"F6.wireOp",EDGE,"E23.9.0.0");var subQ19=makeQuery(id+"F7.opExtrude","CAP_FACE",FACE,{"disambiguationData":[OSD([subQ2,subQ1,subQ18])],"isStart":true});var subQ20=makeQuery(id+"F3.opExtrude","CAP_FACE",FACE,{"disambiguationData":[OSD([sQuery(id+"F2.wireOp",EDGE,"E0"),sQuery(id+"F2.wireOp",EDGE,"E1"),subQ2,sQuery(id+"F2.wireOp",EDGE,"E2.MirrorCS"),sQuery(id+"F2.wireOp",EDGE,"E3.MirrorCS"),subQ1])],"isStart":false});Q0=makeQuery(id+"FuolT4ABAihHTZn_1.boolean.opBoolean","MERGE",FACE,{"derivedFrom":[makeQuery(id+"F7.boolean.opBoolean","SPLIT",FACE,{"disambiguationData":[TD([subQ6,subQ8,makeQuery(id+"F5.opExtrude","SWEPT_FACE",FACE,{"disambiguationData":[OSD([sQuery(id+"F4.wireOp",EDGE,"0306e720-a4cd-40da-927f-c33b378fc5130.MirrorCS")])]}),subQ13,subQ11,subQ7,subQ5,subQ4,subQ12,subQ3,subQ14,subQ16,subQ17,makeQuery(id+"F7.opExtrude","SWEPT_FACE",FACE,{"disambiguationData":[OSD([subQ18])]}),subQ19])],"derivedFrom":subQ20}),makeQuery(id+"F7.boolean.opBoolean","SPLIT",FACE,{"disambiguationData":[TD([subQ6,subQ8,subQ13,subQ11,subQ7,subQ5,subQ4,subQ12,makeQuery(id+"F7.opExtrude","SWEPT_FACE",FACE,{"disambiguationData":[OSD([subQ0])]}),subQ3,subQ10,subQ14,subQ17,subQ19])],"derivedFrom":subQ20}),makeQuery(id+"F7.boolean.opBoolean","SPLIT",FACE,{"disambiguationData":[TD([subQ6,subQ8,subQ13,subQ11,subQ7,subQ5,subQ4,subQ12,subQ3,subQ10,subQ14,subQ16,subQ17,subQ19])],"derivedFrom":subQ20}),makeQuery(id+"FuolT4ABAihHTZn_1.opExtrude","SWEPT_FACE",FACE,{"disambiguationData":[OSD([sQuery(id+"FIxBE3dgotSAZQS_1.wireOp",EDGE,"DbaOr28i-rK8a-sUH4-Cgqk-jCIZV5dNe7y5.bottom")])]})]});}
            var sketch = newSketch(context, id + "F26", { "sketchPlane" : qUnion([Q0])});
            skCircle(sketch, "E66", {"center": v(-23.57, 45) * mm, "radius": 3 * mm});
            skCircle(sketch, "E67", {"center": v(-23.57, 15) * mm, "radius": 3 * mm});
            skCircle(sketch, "E68.MirrorC", {"center": v(23.57, 45) * mm, "radius": 3 * mm});
            skCircle(sketch, "E69.MirrorC", {"center": v(23.57, 15) * mm, "radius": 3 * mm});
            skPoint(sketch, "E70", {"position": v(-23.57, 0) * mm});
            skPoint(sketch, "E71", {"position": v(23.57, 0) * mm});
            skSolve(sketch);
        }
        {
            var Q0;
            Q0=qSketchRegion(id+"F26",true);
            extrude(context, id + "F27", {"entities" : qUnion([Q0]), "operationType" : NewBodyOperationType.REMOVE, "oppositeDirection" : true, "depth" : 25 * mm});
        }
        {
            var Q0;
            {var subQ0=sQuery(id+"F2.wireOp",EDGE,"bd82aa62-3da5-4588-8fb8-dd676fb609a00.MirrorCS");var subQ1=sQuery(id+"F2.wireOp",EDGE,"auNxbXKF-pK2V-sqXS-c08M-DIaJRCpJJF02");var subQ2=sQuery(id+"F6.wireOp",EDGE,"E21");var subQ3=sQuery(id+"F2.wireOp",EDGE,"E1");Q0=makeQuery(id+"F7.boolean.opBoolean","SPLIT",FACE,{"disambiguationData":[TD([makeQuery(id+"F3.opExtrude","SWEPT_FACE",FACE,{"disambiguationData":[OSD([subQ3])]}),makeQuery(id+"F3.opExtrude","SWEPT_FACE",FACE,{"disambiguationData":[OSD([subQ1,subQ0])]}),makeQuery(id+"F5.opExtrude","SWEPT_FACE",FACE,{"disambiguationData":[OSD([sQuery(id+"F4.wireOp",EDGE,"E6")])]}),makeQuery(id+"F5.opExtrude","SWEPT_FACE",FACE,{"disambiguationData":[OSD([sQuery(id+"F4.wireOp",EDGE,"pZRC63if-MIhk-IA8v-DNlQ-6x2yv20jE8mF")])]}),makeQuery(id+"F5.opExtrude","SWEPT_FACE",FACE,{"disambiguationData":[OSD([sQuery(id+"F4.wireOp",EDGE,"QKiYiqoZ-9ux7-oAIY-G16o-4d6qDwNjxzcn")])]}),makeQuery(id+"F7.opExtrude","SWEPT_FACE",FACE,{"disambiguationData":[OSD([subQ2])]}),makeQuery(id+"F7.opExtrude","CAP_FACE",FACE,{"disambiguationData":[OSD([subQ2,sQuery(id+"F6.wireOp",EDGE,"E22")])],"isStart":true}),makeQuery(id+"F7.opExtrude","CAP_FACE",FACE,{"disambiguationData":[OSD([subQ1,subQ0,sQuery(id+"F6.wireOp",EDGE,"E23.1.0.0")])],"isStart":true}),makeQuery(id+"F7.opExtrude","CAP_FACE",FACE,{"disambiguationData":[OSD([subQ1,subQ0,sQuery(id+"F6.wireOp",EDGE,"E23.2.0.0")])],"isStart":true}),makeQuery(id+"F7.opExtrude","CAP_FACE",FACE,{"disambiguationData":[OSD([subQ1,subQ0,sQuery(id+"F6.wireOp",EDGE,"E23.3.0.0")])],"isStart":true}),makeQuery(id+"F7.opExtrude","CAP_FACE",FACE,{"disambiguationData":[OSD([subQ1,subQ0,sQuery(id+"F6.wireOp",EDGE,"E23.4.0.0")])],"isStart":true}),makeQuery(id+"F7.opExtrude","CAP_FACE",FACE,{"disambiguationData":[OSD([subQ1,subQ0,sQuery(id+"F6.wireOp",EDGE,"E23.5.0.0")])],"isStart":true}),makeQuery(id+"F7.opExtrude","CAP_FACE",FACE,{"disambiguationData":[OSD([subQ1,subQ0,sQuery(id+"F6.wireOp",EDGE,"E23.6.0.0")])],"isStart":true}),makeQuery(id+"F7.opExtrude","CAP_FACE",FACE,{"disambiguationData":[OSD([subQ1,subQ0,sQuery(id+"F6.wireOp",EDGE,"E23.7.0.0")])],"isStart":true}),makeQuery(id+"F7.opExtrude","CAP_FACE",FACE,{"disambiguationData":[OSD([subQ1,subQ0,sQuery(id+"F6.wireOp",EDGE,"E23.8.0.0")])],"isStart":true}),makeQuery(id+"F7.opExtrude","CAP_FACE",FACE,{"disambiguationData":[OSD([subQ1,subQ0,sQuery(id+"F6.wireOp",EDGE,"E23.9.0.0")])],"isStart":true})])],"derivedFrom":makeQuery(id+"F3.opExtrude","CAP_FACE",FACE,{"disambiguationData":[OSD([sQuery(id+"F2.wireOp",EDGE,"E0"),subQ3,subQ1,sQuery(id+"F2.wireOp",EDGE,"E2.MirrorCS"),sQuery(id+"F2.wireOp",EDGE,"E3.MirrorCS"),subQ0])],"isStart":false})});}
            var sketch = newSketch(context, id + "F28", { "sketchPlane" : qUnion([Q0])});
            skCircle(sketch, "E72", {"center": v(23.57, 45) * mm, "radius": 5 * mm});
            skCircle(sketch, "E73", {"center": v(-23.57, 45) * mm, "radius": 5 * mm});
            skCircle(sketch, "E74", {"center": v(-23.57, 15) * mm, "radius": 5 * mm});
            skCircle(sketch, "E75", {"center": v(23.57, 15) * mm, "radius": 5 * mm});
            skSolve(sketch);
        }
        {
            var Q0;
            Q0=qSketchRegion(id+"F28",true);
            extrude(context, id + "F29", {"entities" : qUnion([Q0]), "operationType" : NewBodyOperationType.REMOVE, "depth" : 25 * mm});
        }
        {
            var Q0;
            Q0=makeQuery(id+"F3.opExtrude","CAP_FACE",FACE,{"disambiguationData":[OSD([sQuery(id+"F2.wireOp",EDGE,"E0"),sQuery(id+"F2.wireOp",EDGE,"E1"),sQuery(id+"F2.wireOp",EDGE,"auNxbXKF-pK2V-sqXS-c08M-DIaJRCpJJF02"),sQuery(id+"F2.wireOp",EDGE,"E2.MirrorCS"),sQuery(id+"F2.wireOp",EDGE,"E3.MirrorCS"),sQuery(id+"F2.wireOp",EDGE,"bd82aa62-3da5-4588-8fb8-dd676fb609a00.MirrorCS")])],"isStart":true});
            var sketch = newSketch(context, id + "F30", { "sketchPlane" : qUnion([Q0])});
            skLineSegment(sketch, "E76", {"start": v(27.05, 110.22) * mm, "end": v(27.05, 110.22) * mm});
            skPoint(sketch, "E77", {"position": v(-23.57, 15) * mm});
            skLineSegment(sketch, "E78.MirrorCS", {"start": v(-27.05, 110.22) * mm, "end": v(-27.05, 110.22) * mm});
            skPoint(sketch, "E79.MirrorP", {"position": v(23.57, 15) * mm});
            skLineSegment(sketch, "E80", {"start": v(-15.57, 0) * mm, "end": v(-15.57, 60) * mm});
            skLineSegment(sketch, "E81", {"start": v(-15.57, 60) * mm, "end": v(-31.57, 60) * mm});
            skPoint(sketch, "E82", {"position": v(-23.57, 45) * mm});
            skLineSegment(sketch, "E83.MirrorCS", {"start": v(15.57, 60) * mm, "end": v(31.57, 60) * mm});
            skLineSegment(sketch, "E84.MirrorCS", {"start": v(15.57, 0) * mm, "end": v(15.57, 60) * mm});
            skPoint(sketch, "E85", {"position": v(0, 20) * mm});
            skPoint(sketch, "E86", {"position": v(0, 0) * mm});
            skLineSegment(sketch, "E87", {"start": v(-15.57, 0) * mm, "end": v(15.57, 0) * mm});
            skLineSegment(sketch, "E88", {"start": v(31.57, 60) * mm, "end": v(31.57, 0) * mm});
            skLineSegment(sketch, "E89", {"start": v(31.57, 0) * mm, "end": v(60, 0) * mm});
            skLineSegment(sketch, "E90", {"start": v(-31.57, 60) * mm, "end": v(-31.57, 0) * mm});
            skLineSegment(sketch, "E91", {"start": v(-31.57, 0) * mm, "end": v(-60, 0) * mm});
            skLineSegment(sketch, "E92", {"start": v(-60, 0) * mm, "end": v(-60, 40) * mm});
            skLineSegment(sketch, "E93", {"start": v(60, 0) * mm, "end": v(60, 40) * mm});
            skArc(sketch, "E94", {"start": v(60, 40) * mm, "mid": v(51.35, 78.78) * mm, "end": v(27.05, 110.22) * mm});
            skArc(sketch, "E95", {"start": v(-27.05, 110.22) * mm, "mid": v(-51.35, 78.78) * mm, "end": v(-60, 40) * mm});
            skLineSegment(sketch, "E96", {"start": v(-27.05, 110.22) * mm, "end": v(27.05, 110.22) * mm});
            skSolve(sketch);
        }
        {
            var Q0;
            Q0=qSketchRegion(id+"F30",true);
            extrude(context, id + "F31", {"entities" : qUnion([Q0]), "operationType" : NewBodyOperationType.ADD, "depth" : 3 * mm});
        }
        {
            var Q0;
            Q0=makeQuery(id+"F31.opExtrude","CAP_EDGE",EDGE,{"disambiguationData":[OSD([sQuery(id+"F30.wireOp",EDGE,"E76")])],"isStart":false});
            var Q1;
            Q1=makeQuery(id+"F5.opExtrude","CAP_EDGE",EDGE,{"disambiguationData":[OSD([sQuery(id+"F4.wireOp",EDGE,"E6")])],"isStart":false});
            var Q2;
            Q2=makeQuery(id+"F5.opExtrude","CAP_EDGE",EDGE,{"disambiguationData":[OSD([sQuery(id+"F4.wireOp",EDGE,"pZRC63if-MIhk-IA8v-DNlQ-6x2yv20jE8mF")])],"isStart":false});
            var Q3;
            Q3=makeQuery(id+"F5.opExtrude","CAP_EDGE",EDGE,{"disambiguationData":[OSD([sQuery(id+"F4.wireOp",EDGE,"E9")])],"isStart":false});
            var Q4;
            Q4=makeQuery(id+"F5.opExtrude","CAP_EDGE",EDGE,{"disambiguationData":[OSD([sQuery(id+"F4.wireOp",EDGE,"0306e720-a4cd-40da-927f-c33b378fc5130.MirrorCS")])],"isStart":false});
            var Q5;
            Q5=makeQuery(id+"F31.opExtrude","CAP_EDGE",EDGE,{"disambiguationData":[OSD([sQuery(id+"F30.wireOp",EDGE,"RUufvIO7-uwLe-X8pw-0LNw-kXID3cHw8el4")])],"isStart":false});
            var Q6;
            Q6=makeQuery(id+"F31.opExtrude","CAP_EDGE",EDGE,{"disambiguationData":[OSD([sQuery(id+"F30.wireOp",EDGE,"E78.MirrorCS")])],"isStart":false});
            var Q7;
            Q7=makeQuery(id+"F31.opExtrude","CAP_EDGE",EDGE,{"disambiguationData":[OSD([sQuery(id+"F30.wireOp",EDGE,"u4Of9TWJ-UFXE-Kmm3-mw3i-iHo4bxCqP4ZF")])],"isStart":false});
            var Q8;
            Q8=makeQuery(id+"F31.opExtrude","CAP_EDGE",EDGE,{"disambiguationData":[OSD([sQuery(id+"F30.wireOp",EDGE,"SiEx8vhQ-fxaC-5RrE-m7GO-d7uEWHyiGlIe")])],"isStart":false});
            var Q9;
            Q9=makeQuery(id+"F31.opExtrude","CAP_EDGE",EDGE,{"disambiguationData":[OSD([sQuery(id+"F30.wireOp",EDGE,"ykEuGFcq-UQF4-khE9-OFNr-bY3PkPlk7WNo")])],"isStart":false});
            var Q10;
            Q10=makeQuery(id+"F31.boolean.opBoolean","MERGE",EDGE,{"derivedFrom":[makeQuery(id+"F5.boolean.opBoolean","MERGE",EDGE,{"derivedFrom":[makeQuery(id+"F3.opExtrude","SWEPT_EDGE",EDGE,{"disambiguationData":[OSD([sQuery(id+"F2.wireOp",EDGE,"E3.MirrorCS"),sQuery(id+"F2.wireOp",EDGE,"bd82aa62-3da5-4588-8fb8-dd676fb609a00.MirrorCS")])]}),makeQuery(id+"F5.opExtrude","SWEPT_EDGE",EDGE,{"disambiguationData":[OSD([sQuery(id+"F4.wireOp",EDGE,"094a8055-67e1-4fbe-9fcd-0e3f748caa500.MirrorCS"),sQuery(id+"F4.wireOp",EDGE,"E7.MirrorCS")])]})]}),makeQuery(id+"F31.opExtrude","SWEPT_EDGE",EDGE,{"disambiguationData":[OSD([sQuery(id+"F30.wireOp",EDGE,"E78.MirrorCS"),sQuery(id+"F30.wireOp",EDGE,"ykEuGFcq-UQF4-khE9-OFNr-bY3PkPlk7WNo")])]})]});
            var Q11;
            Q11=makeQuery(id+"F31.boolean.opBoolean","MERGE",EDGE,{"derivedFrom":[makeQuery(id+"F5.boolean.opBoolean","MERGE",EDGE,{"derivedFrom":[makeQuery(id+"F3.opExtrude","SWEPT_EDGE",EDGE,{"disambiguationData":[OSD([sQuery(id+"F2.wireOp",EDGE,"E1"),sQuery(id+"F2.wireOp",EDGE,"auNxbXKF-pK2V-sqXS-c08M-DIaJRCpJJF02")])]}),makeQuery(id+"F5.opExtrude","SWEPT_EDGE",EDGE,{"disambiguationData":[OSD([sQuery(id+"F4.wireOp",EDGE,"E6"),sQuery(id+"F4.wireOp",EDGE,"QKiYiqoZ-9ux7-oAIY-G16o-4d6qDwNjxzcn")])]})]}),makeQuery(id+"F31.opExtrude","SWEPT_EDGE",EDGE,{"disambiguationData":[OSD([sQuery(id+"F30.wireOp",EDGE,"E76"),sQuery(id+"F30.wireOp",EDGE,"u4Of9TWJ-UFXE-Kmm3-mw3i-iHo4bxCqP4ZF")])]})]});
            chamfer(context, id + "F32", {"entities" : qUnion([Q0, Q1, Q2, Q3, Q4, Q5, Q6, Q7, Q8, Q9, Q10, Q11]), "width" : 2 * mm, "tangentPropagation" : true});
        }
        {
            var Q0;
            Q0=makeQuery(id+"F31.opExtrude","CAP_EDGE",EDGE,{"disambiguationData":[OSD([sQuery(id+"F30.wireOp",EDGE,"9e28845e-500e-4894-8802-eb7ad12137a14.MirrorCS")])],"isStart":false});
            var Q1;
            Q1=makeQuery(id+"F31.opExtrude","CAP_EDGE",EDGE,{"disambiguationData":[OSD([sQuery(id+"F30.wireOp",EDGE,"E83.MirrorCS")])],"isStart":false});
            var Q2;
            Q2=makeQuery(id+"F31.opExtrude","CAP_EDGE",EDGE,{"disambiguationData":[OSD([sQuery(id+"F30.wireOp",EDGE,"E84.MirrorCS")])],"isStart":false});
            var Q3;
            Q3=makeQuery(id+"F31.opExtrude","CAP_EDGE",EDGE,{"disambiguationData":[OSD([sQuery(id+"F30.wireOp",EDGE,"rDHmkSTM-siCw-gyfN-zfur-uQp36lEMAiwT")])],"isStart":false});
            var Q4;
            Q4=makeQuery(id+"F31.opExtrude","CAP_EDGE",EDGE,{"disambiguationData":[OSD([sQuery(id+"F30.wireOp",EDGE,"E81")])],"isStart":false});
            var Q5;
            Q5=makeQuery(id+"F31.opExtrude","CAP_EDGE",EDGE,{"disambiguationData":[OSD([sQuery(id+"F30.wireOp",EDGE,"E80")])],"isStart":false});
            var Q6;
            Q6=makeQuery(id+"F31.opExtrude","CAP_EDGE",EDGE,{"disambiguationData":[OSD([sQuery(id+"F30.wireOp",EDGE,"E78.MirrorCS")])],"isStart":false});
            var Q7;
            Q7=makeQuery(id+"F31.opExtrude","CAP_EDGE",EDGE,{"disambiguationData":[OSD([sQuery(id+"F30.wireOp",EDGE,"E76")])],"isStart":false});
            var Q8;
            Q8=makeQuery(id+"F31.opExtrude","CAP_EDGE",EDGE,{"disambiguationData":[OSD([sQuery(id+"F30.wireOp",EDGE,"EWeeRF0Z-AfAX-n7vc-ByC2-pyatoFBhdQdW")])],"isStart":false});
            var Q9;
            Q9=makeQuery(id+"F31.opExtrude","CAP_EDGE",EDGE,{"disambiguationData":[OSD([sQuery(id+"F30.wireOp",EDGE,"lQbChSax-9TIr-J5Tv-0UTE-z1H1vQ9YmjyB")])],"isStart":false});
            var Q10;
            Q10=makeQuery(id+"F31.opExtrude","CAP_EDGE",EDGE,{"disambiguationData":[OSD([sQuery(id+"F30.wireOp",EDGE,"E90")])],"isStart":false});
            var Q11;
            Q11=makeQuery(id+"F31.opExtrude","CAP_EDGE",EDGE,{"disambiguationData":[OSD([sQuery(id+"F30.wireOp",EDGE,"E88")])],"isStart":false});
            var Q12;
            Q12=makeQuery(id+"F31.opExtrude","CAP_EDGE",EDGE,{"disambiguationData":[OSD([sQuery(id+"F30.wireOp",EDGE,"E96")])],"isStart":false});
            var Q13;
            Q13=makeQuery(id+"F31.opExtrude","CAP_EDGE",EDGE,{"disambiguationData":[OSD([sQuery(id+"F30.wireOp",EDGE,"E95")])],"isStart":false});
            var Q14;
            Q14=makeQuery(id+"F31.opExtrude","CAP_EDGE",EDGE,{"disambiguationData":[OSD([sQuery(id+"F30.wireOp",EDGE,"E94")])],"isStart":false});
            chamfer(context, id + "F33", {"entities" : qUnion([Q0, Q1, Q2, Q3, Q4, Q5, Q6, Q7, Q8, Q9, Q10, Q11, Q12, Q13, Q14]), "width" : 3 * mm, "tangentPropagation" : true});
        }
        {
            var Q0;
            Q0=makeQuery(id+"F31.opExtrude","CAP_EDGE",EDGE,{"disambiguationData":[OSD([sQuery(id+"F30.wireOp",EDGE,"LmbyR1he-35kO-f53Q-696j-YAIKVnODTwI9")])],"isStart":false});
            var Q1;
            {var subQ0=sQuery(id+"F2.wireOp",EDGE,"bd82aa62-3da5-4588-8fb8-dd676fb609a00.MirrorCS");var subQ1=sQuery(id+"F2.wireOp",EDGE,"auNxbXKF-pK2V-sqXS-c08M-DIaJRCpJJF02");Q1=makeQuery(id+"F33.opChamfer","BLEND_EDGE",EDGE,{"blendedFrom":[makeQuery(id+"F31.opExtrude","CAP_EDGE",EDGE,{"disambiguationData":[OSD([sQuery(id+"F30.wireOp",EDGE,"E80")])],"isStart":false}),makeQuery(id+"F31.boolean.opBoolean","MERGE",FACE,{"derivedFrom":[makeQuery(id+"F7.boolean.opBoolean","MERGE",FACE,{"derivedFrom":[makeQuery(id+"F5.boolean.opBoolean","MERGE",FACE,{"derivedFrom":[makeQuery(id+"F3.opExtrude","SWEPT_FACE",FACE,{"disambiguationData":[OSD([subQ1,subQ0])]}),makeQuery(id+"F5.opExtrude","SWEPT_FACE",FACE,{"disambiguationData":[OSD([sQuery(id+"F4.wireOp",EDGE,"QKiYiqoZ-9ux7-oAIY-G16o-4d6qDwNjxzcn")])]}),makeQuery(id+"F5.opExtrude","SWEPT_FACE",FACE,{"disambiguationData":[OSD([sQuery(id+"F4.wireOp",EDGE,"094a8055-67e1-4fbe-9fcd-0e3f748caa500.MirrorCS")])]})]}),makeQuery(id+"F7.opExtrude","CAP_FACE",FACE,{"disambiguationData":[OSD([sQuery(id+"F6.wireOp",EDGE,"E21"),sQuery(id+"F6.wireOp",EDGE,"E22")])],"isStart":true}),makeQuery(id+"F7.opExtrude","CAP_FACE",FACE,{"disambiguationData":[OSD([subQ1,subQ0,sQuery(id+"F6.wireOp",EDGE,"E23.1.0.0")])],"isStart":true}),makeQuery(id+"F7.opExtrude","CAP_FACE",FACE,{"disambiguationData":[OSD([subQ1,subQ0,sQuery(id+"F6.wireOp",EDGE,"E23.2.0.0")])],"isStart":true}),makeQuery(id+"F7.opExtrude","CAP_FACE",FACE,{"disambiguationData":[OSD([subQ1,subQ0,sQuery(id+"F6.wireOp",EDGE,"E23.3.0.0")])],"isStart":true}),makeQuery(id+"F7.opExtrude","CAP_FACE",FACE,{"disambiguationData":[OSD([subQ1,subQ0,sQuery(id+"F6.wireOp",EDGE,"E23.4.0.0")])],"isStart":true}),makeQuery(id+"F7.opExtrude","CAP_FACE",FACE,{"disambiguationData":[OSD([subQ1,subQ0,sQuery(id+"F6.wireOp",EDGE,"E23.5.0.0")])],"isStart":true}),makeQuery(id+"F7.opExtrude","CAP_FACE",FACE,{"disambiguationData":[OSD([subQ1,subQ0,sQuery(id+"F6.wireOp",EDGE,"E23.6.0.0")])],"isStart":true}),makeQuery(id+"F7.opExtrude","CAP_FACE",FACE,{"disambiguationData":[OSD([subQ1,subQ0,sQuery(id+"F6.wireOp",EDGE,"E23.7.0.0")])],"isStart":true}),makeQuery(id+"F7.opExtrude","CAP_FACE",FACE,{"disambiguationData":[OSD([subQ1,subQ0,sQuery(id+"F6.wireOp",EDGE,"E23.8.0.0")])],"isStart":true}),makeQuery(id+"F7.opExtrude","CAP_FACE",FACE,{"disambiguationData":[OSD([subQ1,subQ0,sQuery(id+"F6.wireOp",EDGE,"E23.9.0.0")])],"isStart":true})]}),makeQuery(id+"F31.opExtrude","SWEPT_FACE",FACE,{"disambiguationData":[OSD([sQuery(id+"F30.wireOp",EDGE,"LmbyR1he-35kO-f53Q-696j-YAIKVnODTwI9")])]}),makeQuery(id+"F31.opExtrude","SWEPT_FACE",FACE,{"disambiguationData":[OSD([sQuery(id+"F30.wireOp",EDGE,"lc0urJVt-xGFD-1UqV-AUzd-Ddt8hkDyLtwQ"),sQuery(id+"F30.wireOp",EDGE,"9e28845e-500e-4894-8802-eb7ad12137a13.MirrorCS")])]}),makeQuery(id+"F31.opExtrude","SWEPT_FACE",FACE,{"disambiguationData":[OSD([sQuery(id+"F30.wireOp",EDGE,"9e28845e-500e-4894-8802-eb7ad12137a10.MirrorCS")])]})]})],"blendedInto":[makeQuery(id+"F31.boolean.opBoolean","MERGE",FACE,{"derivedFrom":[makeQuery(id+"F7.boolean.opBoolean","MERGE",FACE,{"derivedFrom":[makeQuery(id+"F5.boolean.opBoolean","MERGE",FACE,{"derivedFrom":[makeQuery(id+"F3.opExtrude","SWEPT_FACE",FACE,{"disambiguationData":[OSD([subQ1,subQ0])]}),makeQuery(id+"F5.opExtrude","SWEPT_FACE",FACE,{"disambiguationData":[OSD([sQuery(id+"F4.wireOp",EDGE,"QKiYiqoZ-9ux7-oAIY-G16o-4d6qDwNjxzcn")])]}),makeQuery(id+"F5.opExtrude","SWEPT_FACE",FACE,{"disambiguationData":[OSD([sQuery(id+"F4.wireOp",EDGE,"094a8055-67e1-4fbe-9fcd-0e3f748caa500.MirrorCS")])]})]}),makeQuery(id+"F7.opExtrude","CAP_FACE",FACE,{"disambiguationData":[OSD([sQuery(id+"F6.wireOp",EDGE,"E21"),sQuery(id+"F6.wireOp",EDGE,"E22")])],"isStart":true}),makeQuery(id+"F7.opExtrude","CAP_FACE",FACE,{"disambiguationData":[OSD([subQ1,subQ0,sQuery(id+"F6.wireOp",EDGE,"E23.1.0.0")])],"isStart":true}),makeQuery(id+"F7.opExtrude","CAP_FACE",FACE,{"disambiguationData":[OSD([subQ1,subQ0,sQuery(id+"F6.wireOp",EDGE,"E23.2.0.0")])],"isStart":true}),makeQuery(id+"F7.opExtrude","CAP_FACE",FACE,{"disambiguationData":[OSD([subQ1,subQ0,sQuery(id+"F6.wireOp",EDGE,"E23.3.0.0")])],"isStart":true}),makeQuery(id+"F7.opExtrude","CAP_FACE",FACE,{"disambiguationData":[OSD([subQ1,subQ0,sQuery(id+"F6.wireOp",EDGE,"E23.4.0.0")])],"isStart":true}),makeQuery(id+"F7.opExtrude","CAP_FACE",FACE,{"disambiguationData":[OSD([subQ1,subQ0,sQuery(id+"F6.wireOp",EDGE,"E23.5.0.0")])],"isStart":true}),makeQuery(id+"F7.opExtrude","CAP_FACE",FACE,{"disambiguationData":[OSD([subQ1,subQ0,sQuery(id+"F6.wireOp",EDGE,"E23.6.0.0")])],"isStart":true}),makeQuery(id+"F7.opExtrude","CAP_FACE",FACE,{"disambiguationData":[OSD([subQ1,subQ0,sQuery(id+"F6.wireOp",EDGE,"E23.7.0.0")])],"isStart":true}),makeQuery(id+"F7.opExtrude","CAP_FACE",FACE,{"disambiguationData":[OSD([subQ1,subQ0,sQuery(id+"F6.wireOp",EDGE,"E23.8.0.0")])],"isStart":true}),makeQuery(id+"F7.opExtrude","CAP_FACE",FACE,{"disambiguationData":[OSD([subQ1,subQ0,sQuery(id+"F6.wireOp",EDGE,"E23.9.0.0")])],"isStart":true})]}),makeQuery(id+"F31.opExtrude","SWEPT_FACE",FACE,{"disambiguationData":[OSD([sQuery(id+"F30.wireOp",EDGE,"LmbyR1he-35kO-f53Q-696j-YAIKVnODTwI9")])]}),makeQuery(id+"F31.opExtrude","SWEPT_FACE",FACE,{"disambiguationData":[OSD([sQuery(id+"F30.wireOp",EDGE,"lc0urJVt-xGFD-1UqV-AUzd-Ddt8hkDyLtwQ"),sQuery(id+"F30.wireOp",EDGE,"9e28845e-500e-4894-8802-eb7ad12137a13.MirrorCS")])]}),makeQuery(id+"F31.opExtrude","SWEPT_FACE",FACE,{"disambiguationData":[OSD([sQuery(id+"F30.wireOp",EDGE,"9e28845e-500e-4894-8802-eb7ad12137a10.MirrorCS")])]})]})]});}
            var Q2;
            {var subQ0=sQuery(id+"F2.wireOp",EDGE,"bd82aa62-3da5-4588-8fb8-dd676fb609a00.MirrorCS");var subQ1=sQuery(id+"F2.wireOp",EDGE,"auNxbXKF-pK2V-sqXS-c08M-DIaJRCpJJF02");Q2=makeQuery(id+"F31.boolean.opBoolean","SPLIT",EDGE,{"disambiguationData":[TD([makeQuery(id+"F31.opExtrude","SWEPT_FACE",FACE,{"disambiguationData":[OSD([sQuery(id+"F30.wireOp",EDGE,"rDHmkSTM-siCw-gyfN-zfur-uQp36lEMAiwT")])]})])],"derivedFrom":makeQuery(id+"F3.opExtrude","CAP_EDGE",EDGE,{"disambiguationData":[OSD([subQ1,subQ0])],"isStart":true})});}
            var Q3;
            {var subQ0=sQuery(id+"F2.wireOp",EDGE,"bd82aa62-3da5-4588-8fb8-dd676fb609a00.MirrorCS");var subQ1=sQuery(id+"F2.wireOp",EDGE,"auNxbXKF-pK2V-sqXS-c08M-DIaJRCpJJF02");Q3=makeQuery(id+"F33.opChamfer","BLEND_EDGE",EDGE,{"blendedFrom":[makeQuery(id+"F31.opExtrude","CAP_EDGE",EDGE,{"disambiguationData":[OSD([sQuery(id+"F30.wireOp",EDGE,"rDHmkSTM-siCw-gyfN-zfur-uQp36lEMAiwT")])],"isStart":false}),makeQuery(id+"F31.boolean.opBoolean","MERGE",FACE,{"derivedFrom":[makeQuery(id+"F7.boolean.opBoolean","MERGE",FACE,{"derivedFrom":[makeQuery(id+"F5.boolean.opBoolean","MERGE",FACE,{"derivedFrom":[makeQuery(id+"F3.opExtrude","SWEPT_FACE",FACE,{"disambiguationData":[OSD([subQ1,subQ0])]}),makeQuery(id+"F5.opExtrude","SWEPT_FACE",FACE,{"disambiguationData":[OSD([sQuery(id+"F4.wireOp",EDGE,"QKiYiqoZ-9ux7-oAIY-G16o-4d6qDwNjxzcn")])]}),makeQuery(id+"F5.opExtrude","SWEPT_FACE",FACE,{"disambiguationData":[OSD([sQuery(id+"F4.wireOp",EDGE,"094a8055-67e1-4fbe-9fcd-0e3f748caa500.MirrorCS")])]})]}),makeQuery(id+"F7.opExtrude","CAP_FACE",FACE,{"disambiguationData":[OSD([sQuery(id+"F6.wireOp",EDGE,"E21"),sQuery(id+"F6.wireOp",EDGE,"E22")])],"isStart":true}),makeQuery(id+"F7.opExtrude","CAP_FACE",FACE,{"disambiguationData":[OSD([subQ1,subQ0,sQuery(id+"F6.wireOp",EDGE,"E23.1.0.0")])],"isStart":true}),makeQuery(id+"F7.opExtrude","CAP_FACE",FACE,{"disambiguationData":[OSD([subQ1,subQ0,sQuery(id+"F6.wireOp",EDGE,"E23.2.0.0")])],"isStart":true}),makeQuery(id+"F7.opExtrude","CAP_FACE",FACE,{"disambiguationData":[OSD([subQ1,subQ0,sQuery(id+"F6.wireOp",EDGE,"E23.3.0.0")])],"isStart":true}),makeQuery(id+"F7.opExtrude","CAP_FACE",FACE,{"disambiguationData":[OSD([subQ1,subQ0,sQuery(id+"F6.wireOp",EDGE,"E23.4.0.0")])],"isStart":true}),makeQuery(id+"F7.opExtrude","CAP_FACE",FACE,{"disambiguationData":[OSD([subQ1,subQ0,sQuery(id+"F6.wireOp",EDGE,"E23.5.0.0")])],"isStart":true}),makeQuery(id+"F7.opExtrude","CAP_FACE",FACE,{"disambiguationData":[OSD([subQ1,subQ0,sQuery(id+"F6.wireOp",EDGE,"E23.6.0.0")])],"isStart":true}),makeQuery(id+"F7.opExtrude","CAP_FACE",FACE,{"disambiguationData":[OSD([subQ1,subQ0,sQuery(id+"F6.wireOp",EDGE,"E23.7.0.0")])],"isStart":true}),makeQuery(id+"F7.opExtrude","CAP_FACE",FACE,{"disambiguationData":[OSD([subQ1,subQ0,sQuery(id+"F6.wireOp",EDGE,"E23.8.0.0")])],"isStart":true}),makeQuery(id+"F7.opExtrude","CAP_FACE",FACE,{"disambiguationData":[OSD([subQ1,subQ0,sQuery(id+"F6.wireOp",EDGE,"E23.9.0.0")])],"isStart":true})]}),makeQuery(id+"F31.opExtrude","SWEPT_FACE",FACE,{"disambiguationData":[OSD([sQuery(id+"F30.wireOp",EDGE,"LmbyR1he-35kO-f53Q-696j-YAIKVnODTwI9")])]}),makeQuery(id+"F31.opExtrude","SWEPT_FACE",FACE,{"disambiguationData":[OSD([sQuery(id+"F30.wireOp",EDGE,"lc0urJVt-xGFD-1UqV-AUzd-Ddt8hkDyLtwQ"),sQuery(id+"F30.wireOp",EDGE,"9e28845e-500e-4894-8802-eb7ad12137a13.MirrorCS")])]}),makeQuery(id+"F31.opExtrude","SWEPT_FACE",FACE,{"disambiguationData":[OSD([sQuery(id+"F30.wireOp",EDGE,"9e28845e-500e-4894-8802-eb7ad12137a10.MirrorCS")])]})]})],"blendedInto":[makeQuery(id+"F31.boolean.opBoolean","MERGE",FACE,{"derivedFrom":[makeQuery(id+"F7.boolean.opBoolean","MERGE",FACE,{"derivedFrom":[makeQuery(id+"F5.boolean.opBoolean","MERGE",FACE,{"derivedFrom":[makeQuery(id+"F3.opExtrude","SWEPT_FACE",FACE,{"disambiguationData":[OSD([subQ1,subQ0])]}),makeQuery(id+"F5.opExtrude","SWEPT_FACE",FACE,{"disambiguationData":[OSD([sQuery(id+"F4.wireOp",EDGE,"QKiYiqoZ-9ux7-oAIY-G16o-4d6qDwNjxzcn")])]}),makeQuery(id+"F5.opExtrude","SWEPT_FACE",FACE,{"disambiguationData":[OSD([sQuery(id+"F4.wireOp",EDGE,"094a8055-67e1-4fbe-9fcd-0e3f748caa500.MirrorCS")])]})]}),makeQuery(id+"F7.opExtrude","CAP_FACE",FACE,{"disambiguationData":[OSD([sQuery(id+"F6.wireOp",EDGE,"E21"),sQuery(id+"F6.wireOp",EDGE,"E22")])],"isStart":true}),makeQuery(id+"F7.opExtrude","CAP_FACE",FACE,{"disambiguationData":[OSD([subQ1,subQ0,sQuery(id+"F6.wireOp",EDGE,"E23.1.0.0")])],"isStart":true}),makeQuery(id+"F7.opExtrude","CAP_FACE",FACE,{"disambiguationData":[OSD([subQ1,subQ0,sQuery(id+"F6.wireOp",EDGE,"E23.2.0.0")])],"isStart":true}),makeQuery(id+"F7.opExtrude","CAP_FACE",FACE,{"disambiguationData":[OSD([subQ1,subQ0,sQuery(id+"F6.wireOp",EDGE,"E23.3.0.0")])],"isStart":true}),makeQuery(id+"F7.opExtrude","CAP_FACE",FACE,{"disambiguationData":[OSD([subQ1,subQ0,sQuery(id+"F6.wireOp",EDGE,"E23.4.0.0")])],"isStart":true}),makeQuery(id+"F7.opExtrude","CAP_FACE",FACE,{"disambiguationData":[OSD([subQ1,subQ0,sQuery(id+"F6.wireOp",EDGE,"E23.5.0.0")])],"isStart":true}),makeQuery(id+"F7.opExtrude","CAP_FACE",FACE,{"disambiguationData":[OSD([subQ1,subQ0,sQuery(id+"F6.wireOp",EDGE,"E23.6.0.0")])],"isStart":true}),makeQuery(id+"F7.opExtrude","CAP_FACE",FACE,{"disambiguationData":[OSD([subQ1,subQ0,sQuery(id+"F6.wireOp",EDGE,"E23.7.0.0")])],"isStart":true}),makeQuery(id+"F7.opExtrude","CAP_FACE",FACE,{"disambiguationData":[OSD([subQ1,subQ0,sQuery(id+"F6.wireOp",EDGE,"E23.8.0.0")])],"isStart":true}),makeQuery(id+"F7.opExtrude","CAP_FACE",FACE,{"disambiguationData":[OSD([subQ1,subQ0,sQuery(id+"F6.wireOp",EDGE,"E23.9.0.0")])],"isStart":true})]}),makeQuery(id+"F31.opExtrude","SWEPT_FACE",FACE,{"disambiguationData":[OSD([sQuery(id+"F30.wireOp",EDGE,"LmbyR1he-35kO-f53Q-696j-YAIKVnODTwI9")])]}),makeQuery(id+"F31.opExtrude","SWEPT_FACE",FACE,{"disambiguationData":[OSD([sQuery(id+"F30.wireOp",EDGE,"lc0urJVt-xGFD-1UqV-AUzd-Ddt8hkDyLtwQ"),sQuery(id+"F30.wireOp",EDGE,"9e28845e-500e-4894-8802-eb7ad12137a13.MirrorCS")])]}),makeQuery(id+"F31.opExtrude","SWEPT_FACE",FACE,{"disambiguationData":[OSD([sQuery(id+"F30.wireOp",EDGE,"9e28845e-500e-4894-8802-eb7ad12137a10.MirrorCS")])]})]})]});}
            var Q4;
            Q4=makeQuery(id+"F31.opExtrude","CAP_EDGE",EDGE,{"disambiguationData":[OSD([sQuery(id+"F30.wireOp",EDGE,"lc0urJVt-xGFD-1UqV-AUzd-Ddt8hkDyLtwQ"),sQuery(id+"F30.wireOp",EDGE,"9e28845e-500e-4894-8802-eb7ad12137a13.MirrorCS")])],"isStart":false});
            var Q5;
            {var subQ0=sQuery(id+"F2.wireOp",EDGE,"bd82aa62-3da5-4588-8fb8-dd676fb609a00.MirrorCS");var subQ1=sQuery(id+"F2.wireOp",EDGE,"auNxbXKF-pK2V-sqXS-c08M-DIaJRCpJJF02");Q5=makeQuery(id+"F33.opChamfer","BLEND_EDGE",EDGE,{"blendedFrom":[makeQuery(id+"F31.opExtrude","CAP_EDGE",EDGE,{"disambiguationData":[OSD([sQuery(id+"F30.wireOp",EDGE,"9e28845e-500e-4894-8802-eb7ad12137a14.MirrorCS")])],"isStart":false}),makeQuery(id+"F31.boolean.opBoolean","MERGE",FACE,{"derivedFrom":[makeQuery(id+"F7.boolean.opBoolean","MERGE",FACE,{"derivedFrom":[makeQuery(id+"F5.boolean.opBoolean","MERGE",FACE,{"derivedFrom":[makeQuery(id+"F3.opExtrude","SWEPT_FACE",FACE,{"disambiguationData":[OSD([subQ1,subQ0])]}),makeQuery(id+"F5.opExtrude","SWEPT_FACE",FACE,{"disambiguationData":[OSD([sQuery(id+"F4.wireOp",EDGE,"QKiYiqoZ-9ux7-oAIY-G16o-4d6qDwNjxzcn")])]}),makeQuery(id+"F5.opExtrude","SWEPT_FACE",FACE,{"disambiguationData":[OSD([sQuery(id+"F4.wireOp",EDGE,"094a8055-67e1-4fbe-9fcd-0e3f748caa500.MirrorCS")])]})]}),makeQuery(id+"F7.opExtrude","CAP_FACE",FACE,{"disambiguationData":[OSD([sQuery(id+"F6.wireOp",EDGE,"E21"),sQuery(id+"F6.wireOp",EDGE,"E22")])],"isStart":true}),makeQuery(id+"F7.opExtrude","CAP_FACE",FACE,{"disambiguationData":[OSD([subQ1,subQ0,sQuery(id+"F6.wireOp",EDGE,"E23.1.0.0")])],"isStart":true}),makeQuery(id+"F7.opExtrude","CAP_FACE",FACE,{"disambiguationData":[OSD([subQ1,subQ0,sQuery(id+"F6.wireOp",EDGE,"E23.2.0.0")])],"isStart":true}),makeQuery(id+"F7.opExtrude","CAP_FACE",FACE,{"disambiguationData":[OSD([subQ1,subQ0,sQuery(id+"F6.wireOp",EDGE,"E23.3.0.0")])],"isStart":true}),makeQuery(id+"F7.opExtrude","CAP_FACE",FACE,{"disambiguationData":[OSD([subQ1,subQ0,sQuery(id+"F6.wireOp",EDGE,"E23.4.0.0")])],"isStart":true}),makeQuery(id+"F7.opExtrude","CAP_FACE",FACE,{"disambiguationData":[OSD([subQ1,subQ0,sQuery(id+"F6.wireOp",EDGE,"E23.5.0.0")])],"isStart":true}),makeQuery(id+"F7.opExtrude","CAP_FACE",FACE,{"disambiguationData":[OSD([subQ1,subQ0,sQuery(id+"F6.wireOp",EDGE,"E23.6.0.0")])],"isStart":true}),makeQuery(id+"F7.opExtrude","CAP_FACE",FACE,{"disambiguationData":[OSD([subQ1,subQ0,sQuery(id+"F6.wireOp",EDGE,"E23.7.0.0")])],"isStart":true}),makeQuery(id+"F7.opExtrude","CAP_FACE",FACE,{"disambiguationData":[OSD([subQ1,subQ0,sQuery(id+"F6.wireOp",EDGE,"E23.8.0.0")])],"isStart":true}),makeQuery(id+"F7.opExtrude","CAP_FACE",FACE,{"disambiguationData":[OSD([subQ1,subQ0,sQuery(id+"F6.wireOp",EDGE,"E23.9.0.0")])],"isStart":true})]}),makeQuery(id+"F31.opExtrude","SWEPT_FACE",FACE,{"disambiguationData":[OSD([sQuery(id+"F30.wireOp",EDGE,"LmbyR1he-35kO-f53Q-696j-YAIKVnODTwI9")])]}),makeQuery(id+"F31.opExtrude","SWEPT_FACE",FACE,{"disambiguationData":[OSD([sQuery(id+"F30.wireOp",EDGE,"lc0urJVt-xGFD-1UqV-AUzd-Ddt8hkDyLtwQ"),sQuery(id+"F30.wireOp",EDGE,"9e28845e-500e-4894-8802-eb7ad12137a13.MirrorCS")])]}),makeQuery(id+"F31.opExtrude","SWEPT_FACE",FACE,{"disambiguationData":[OSD([sQuery(id+"F30.wireOp",EDGE,"9e28845e-500e-4894-8802-eb7ad12137a10.MirrorCS")])]})]})],"blendedInto":[makeQuery(id+"F31.boolean.opBoolean","MERGE",FACE,{"derivedFrom":[makeQuery(id+"F7.boolean.opBoolean","MERGE",FACE,{"derivedFrom":[makeQuery(id+"F5.boolean.opBoolean","MERGE",FACE,{"derivedFrom":[makeQuery(id+"F3.opExtrude","SWEPT_FACE",FACE,{"disambiguationData":[OSD([subQ1,subQ0])]}),makeQuery(id+"F5.opExtrude","SWEPT_FACE",FACE,{"disambiguationData":[OSD([sQuery(id+"F4.wireOp",EDGE,"QKiYiqoZ-9ux7-oAIY-G16o-4d6qDwNjxzcn")])]}),makeQuery(id+"F5.opExtrude","SWEPT_FACE",FACE,{"disambiguationData":[OSD([sQuery(id+"F4.wireOp",EDGE,"094a8055-67e1-4fbe-9fcd-0e3f748caa500.MirrorCS")])]})]}),makeQuery(id+"F7.opExtrude","CAP_FACE",FACE,{"disambiguationData":[OSD([sQuery(id+"F6.wireOp",EDGE,"E21"),sQuery(id+"F6.wireOp",EDGE,"E22")])],"isStart":true}),makeQuery(id+"F7.opExtrude","CAP_FACE",FACE,{"disambiguationData":[OSD([subQ1,subQ0,sQuery(id+"F6.wireOp",EDGE,"E23.1.0.0")])],"isStart":true}),makeQuery(id+"F7.opExtrude","CAP_FACE",FACE,{"disambiguationData":[OSD([subQ1,subQ0,sQuery(id+"F6.wireOp",EDGE,"E23.2.0.0")])],"isStart":true}),makeQuery(id+"F7.opExtrude","CAP_FACE",FACE,{"disambiguationData":[OSD([subQ1,subQ0,sQuery(id+"F6.wireOp",EDGE,"E23.3.0.0")])],"isStart":true}),makeQuery(id+"F7.opExtrude","CAP_FACE",FACE,{"disambiguationData":[OSD([subQ1,subQ0,sQuery(id+"F6.wireOp",EDGE,"E23.4.0.0")])],"isStart":true}),makeQuery(id+"F7.opExtrude","CAP_FACE",FACE,{"disambiguationData":[OSD([subQ1,subQ0,sQuery(id+"F6.wireOp",EDGE,"E23.5.0.0")])],"isStart":true}),makeQuery(id+"F7.opExtrude","CAP_FACE",FACE,{"disambiguationData":[OSD([subQ1,subQ0,sQuery(id+"F6.wireOp",EDGE,"E23.6.0.0")])],"isStart":true}),makeQuery(id+"F7.opExtrude","CAP_FACE",FACE,{"disambiguationData":[OSD([subQ1,subQ0,sQuery(id+"F6.wireOp",EDGE,"E23.7.0.0")])],"isStart":true}),makeQuery(id+"F7.opExtrude","CAP_FACE",FACE,{"disambiguationData":[OSD([subQ1,subQ0,sQuery(id+"F6.wireOp",EDGE,"E23.8.0.0")])],"isStart":true}),makeQuery(id+"F7.opExtrude","CAP_FACE",FACE,{"disambiguationData":[OSD([subQ1,subQ0,sQuery(id+"F6.wireOp",EDGE,"E23.9.0.0")])],"isStart":true})]}),makeQuery(id+"F31.opExtrude","SWEPT_FACE",FACE,{"disambiguationData":[OSD([sQuery(id+"F30.wireOp",EDGE,"LmbyR1he-35kO-f53Q-696j-YAIKVnODTwI9")])]}),makeQuery(id+"F31.opExtrude","SWEPT_FACE",FACE,{"disambiguationData":[OSD([sQuery(id+"F30.wireOp",EDGE,"lc0urJVt-xGFD-1UqV-AUzd-Ddt8hkDyLtwQ"),sQuery(id+"F30.wireOp",EDGE,"9e28845e-500e-4894-8802-eb7ad12137a13.MirrorCS")])]}),makeQuery(id+"F31.opExtrude","SWEPT_FACE",FACE,{"disambiguationData":[OSD([sQuery(id+"F30.wireOp",EDGE,"9e28845e-500e-4894-8802-eb7ad12137a10.MirrorCS")])]})]})]});}
            var Q6;
            {var subQ0=sQuery(id+"F2.wireOp",EDGE,"bd82aa62-3da5-4588-8fb8-dd676fb609a00.MirrorCS");var subQ1=sQuery(id+"F2.wireOp",EDGE,"auNxbXKF-pK2V-sqXS-c08M-DIaJRCpJJF02");Q6=makeQuery(id+"F31.boolean.opBoolean","SPLIT",EDGE,{"disambiguationData":[TD([makeQuery(id+"F31.opExtrude","SWEPT_FACE",FACE,{"disambiguationData":[OSD([sQuery(id+"F30.wireOp",EDGE,"9e28845e-500e-4894-8802-eb7ad12137a14.MirrorCS")])]})])],"derivedFrom":makeQuery(id+"F3.opExtrude","CAP_EDGE",EDGE,{"disambiguationData":[OSD([subQ1,subQ0])],"isStart":true})});}
            var Q7;
            {var subQ0=sQuery(id+"F2.wireOp",EDGE,"bd82aa62-3da5-4588-8fb8-dd676fb609a00.MirrorCS");var subQ1=sQuery(id+"F2.wireOp",EDGE,"auNxbXKF-pK2V-sqXS-c08M-DIaJRCpJJF02");Q7=makeQuery(id+"F33.opChamfer","BLEND_EDGE",EDGE,{"blendedFrom":[makeQuery(id+"F31.opExtrude","CAP_EDGE",EDGE,{"disambiguationData":[OSD([sQuery(id+"F30.wireOp",EDGE,"E84.MirrorCS")])],"isStart":false}),makeQuery(id+"F31.boolean.opBoolean","MERGE",FACE,{"derivedFrom":[makeQuery(id+"F7.boolean.opBoolean","MERGE",FACE,{"derivedFrom":[makeQuery(id+"F5.boolean.opBoolean","MERGE",FACE,{"derivedFrom":[makeQuery(id+"F3.opExtrude","SWEPT_FACE",FACE,{"disambiguationData":[OSD([subQ1,subQ0])]}),makeQuery(id+"F5.opExtrude","SWEPT_FACE",FACE,{"disambiguationData":[OSD([sQuery(id+"F4.wireOp",EDGE,"QKiYiqoZ-9ux7-oAIY-G16o-4d6qDwNjxzcn")])]}),makeQuery(id+"F5.opExtrude","SWEPT_FACE",FACE,{"disambiguationData":[OSD([sQuery(id+"F4.wireOp",EDGE,"094a8055-67e1-4fbe-9fcd-0e3f748caa500.MirrorCS")])]})]}),makeQuery(id+"F7.opExtrude","CAP_FACE",FACE,{"disambiguationData":[OSD([sQuery(id+"F6.wireOp",EDGE,"E21"),sQuery(id+"F6.wireOp",EDGE,"E22")])],"isStart":true}),makeQuery(id+"F7.opExtrude","CAP_FACE",FACE,{"disambiguationData":[OSD([subQ1,subQ0,sQuery(id+"F6.wireOp",EDGE,"E23.1.0.0")])],"isStart":true}),makeQuery(id+"F7.opExtrude","CAP_FACE",FACE,{"disambiguationData":[OSD([subQ1,subQ0,sQuery(id+"F6.wireOp",EDGE,"E23.2.0.0")])],"isStart":true}),makeQuery(id+"F7.opExtrude","CAP_FACE",FACE,{"disambiguationData":[OSD([subQ1,subQ0,sQuery(id+"F6.wireOp",EDGE,"E23.3.0.0")])],"isStart":true}),makeQuery(id+"F7.opExtrude","CAP_FACE",FACE,{"disambiguationData":[OSD([subQ1,subQ0,sQuery(id+"F6.wireOp",EDGE,"E23.4.0.0")])],"isStart":true}),makeQuery(id+"F7.opExtrude","CAP_FACE",FACE,{"disambiguationData":[OSD([subQ1,subQ0,sQuery(id+"F6.wireOp",EDGE,"E23.5.0.0")])],"isStart":true}),makeQuery(id+"F7.opExtrude","CAP_FACE",FACE,{"disambiguationData":[OSD([subQ1,subQ0,sQuery(id+"F6.wireOp",EDGE,"E23.6.0.0")])],"isStart":true}),makeQuery(id+"F7.opExtrude","CAP_FACE",FACE,{"disambiguationData":[OSD([subQ1,subQ0,sQuery(id+"F6.wireOp",EDGE,"E23.7.0.0")])],"isStart":true}),makeQuery(id+"F7.opExtrude","CAP_FACE",FACE,{"disambiguationData":[OSD([subQ1,subQ0,sQuery(id+"F6.wireOp",EDGE,"E23.8.0.0")])],"isStart":true}),makeQuery(id+"F7.opExtrude","CAP_FACE",FACE,{"disambiguationData":[OSD([subQ1,subQ0,sQuery(id+"F6.wireOp",EDGE,"E23.9.0.0")])],"isStart":true})]}),makeQuery(id+"F31.opExtrude","SWEPT_FACE",FACE,{"disambiguationData":[OSD([sQuery(id+"F30.wireOp",EDGE,"LmbyR1he-35kO-f53Q-696j-YAIKVnODTwI9")])]}),makeQuery(id+"F31.opExtrude","SWEPT_FACE",FACE,{"disambiguationData":[OSD([sQuery(id+"F30.wireOp",EDGE,"lc0urJVt-xGFD-1UqV-AUzd-Ddt8hkDyLtwQ"),sQuery(id+"F30.wireOp",EDGE,"9e28845e-500e-4894-8802-eb7ad12137a13.MirrorCS")])]}),makeQuery(id+"F31.opExtrude","SWEPT_FACE",FACE,{"disambiguationData":[OSD([sQuery(id+"F30.wireOp",EDGE,"9e28845e-500e-4894-8802-eb7ad12137a10.MirrorCS")])]})]})],"blendedInto":[makeQuery(id+"F31.boolean.opBoolean","MERGE",FACE,{"derivedFrom":[makeQuery(id+"F7.boolean.opBoolean","MERGE",FACE,{"derivedFrom":[makeQuery(id+"F5.boolean.opBoolean","MERGE",FACE,{"derivedFrom":[makeQuery(id+"F3.opExtrude","SWEPT_FACE",FACE,{"disambiguationData":[OSD([subQ1,subQ0])]}),makeQuery(id+"F5.opExtrude","SWEPT_FACE",FACE,{"disambiguationData":[OSD([sQuery(id+"F4.wireOp",EDGE,"QKiYiqoZ-9ux7-oAIY-G16o-4d6qDwNjxzcn")])]}),makeQuery(id+"F5.opExtrude","SWEPT_FACE",FACE,{"disambiguationData":[OSD([sQuery(id+"F4.wireOp",EDGE,"094a8055-67e1-4fbe-9fcd-0e3f748caa500.MirrorCS")])]})]}),makeQuery(id+"F7.opExtrude","CAP_FACE",FACE,{"disambiguationData":[OSD([sQuery(id+"F6.wireOp",EDGE,"E21"),sQuery(id+"F6.wireOp",EDGE,"E22")])],"isStart":true}),makeQuery(id+"F7.opExtrude","CAP_FACE",FACE,{"disambiguationData":[OSD([subQ1,subQ0,sQuery(id+"F6.wireOp",EDGE,"E23.1.0.0")])],"isStart":true}),makeQuery(id+"F7.opExtrude","CAP_FACE",FACE,{"disambiguationData":[OSD([subQ1,subQ0,sQuery(id+"F6.wireOp",EDGE,"E23.2.0.0")])],"isStart":true}),makeQuery(id+"F7.opExtrude","CAP_FACE",FACE,{"disambiguationData":[OSD([subQ1,subQ0,sQuery(id+"F6.wireOp",EDGE,"E23.3.0.0")])],"isStart":true}),makeQuery(id+"F7.opExtrude","CAP_FACE",FACE,{"disambiguationData":[OSD([subQ1,subQ0,sQuery(id+"F6.wireOp",EDGE,"E23.4.0.0")])],"isStart":true}),makeQuery(id+"F7.opExtrude","CAP_FACE",FACE,{"disambiguationData":[OSD([subQ1,subQ0,sQuery(id+"F6.wireOp",EDGE,"E23.5.0.0")])],"isStart":true}),makeQuery(id+"F7.opExtrude","CAP_FACE",FACE,{"disambiguationData":[OSD([subQ1,subQ0,sQuery(id+"F6.wireOp",EDGE,"E23.6.0.0")])],"isStart":true}),makeQuery(id+"F7.opExtrude","CAP_FACE",FACE,{"disambiguationData":[OSD([subQ1,subQ0,sQuery(id+"F6.wireOp",EDGE,"E23.7.0.0")])],"isStart":true}),makeQuery(id+"F7.opExtrude","CAP_FACE",FACE,{"disambiguationData":[OSD([subQ1,subQ0,sQuery(id+"F6.wireOp",EDGE,"E23.8.0.0")])],"isStart":true}),makeQuery(id+"F7.opExtrude","CAP_FACE",FACE,{"disambiguationData":[OSD([subQ1,subQ0,sQuery(id+"F6.wireOp",EDGE,"E23.9.0.0")])],"isStart":true})]}),makeQuery(id+"F31.opExtrude","SWEPT_FACE",FACE,{"disambiguationData":[OSD([sQuery(id+"F30.wireOp",EDGE,"LmbyR1he-35kO-f53Q-696j-YAIKVnODTwI9")])]}),makeQuery(id+"F31.opExtrude","SWEPT_FACE",FACE,{"disambiguationData":[OSD([sQuery(id+"F30.wireOp",EDGE,"lc0urJVt-xGFD-1UqV-AUzd-Ddt8hkDyLtwQ"),sQuery(id+"F30.wireOp",EDGE,"9e28845e-500e-4894-8802-eb7ad12137a13.MirrorCS")])]}),makeQuery(id+"F31.opExtrude","SWEPT_FACE",FACE,{"disambiguationData":[OSD([sQuery(id+"F30.wireOp",EDGE,"9e28845e-500e-4894-8802-eb7ad12137a10.MirrorCS")])]})]})]});}
            var Q8;
            Q8=makeQuery(id+"F31.opExtrude","CAP_EDGE",EDGE,{"disambiguationData":[OSD([sQuery(id+"F30.wireOp",EDGE,"9e28845e-500e-4894-8802-eb7ad12137a10.MirrorCS")])],"isStart":false});
            var Q9;
            {var subQ0=sQuery(id+"F2.wireOp",EDGE,"bd82aa62-3da5-4588-8fb8-dd676fb609a00.MirrorCS");var subQ1=sQuery(id+"F2.wireOp",EDGE,"auNxbXKF-pK2V-sqXS-c08M-DIaJRCpJJF02");Q9=makeQuery(id+"F33.opChamfer","BLEND_EDGE",EDGE,{"blendedFrom":[makeQuery(id+"F31.opExtrude","CAP_EDGE",EDGE,{"disambiguationData":[OSD([sQuery(id+"F30.wireOp",EDGE,"E76")])],"isStart":false}),makeQuery(id+"F31.boolean.opBoolean","MERGE",FACE,{"derivedFrom":[makeQuery(id+"F7.boolean.opBoolean","MERGE",FACE,{"derivedFrom":[makeQuery(id+"F5.boolean.opBoolean","MERGE",FACE,{"derivedFrom":[makeQuery(id+"F3.opExtrude","SWEPT_FACE",FACE,{"disambiguationData":[OSD([subQ1,subQ0])]}),makeQuery(id+"F5.opExtrude","SWEPT_FACE",FACE,{"disambiguationData":[OSD([sQuery(id+"F4.wireOp",EDGE,"QKiYiqoZ-9ux7-oAIY-G16o-4d6qDwNjxzcn")])]}),makeQuery(id+"F5.opExtrude","SWEPT_FACE",FACE,{"disambiguationData":[OSD([sQuery(id+"F4.wireOp",EDGE,"094a8055-67e1-4fbe-9fcd-0e3f748caa500.MirrorCS")])]})]}),makeQuery(id+"F7.opExtrude","CAP_FACE",FACE,{"disambiguationData":[OSD([sQuery(id+"F6.wireOp",EDGE,"E21"),sQuery(id+"F6.wireOp",EDGE,"E22")])],"isStart":true}),makeQuery(id+"F7.opExtrude","CAP_FACE",FACE,{"disambiguationData":[OSD([subQ1,subQ0,sQuery(id+"F6.wireOp",EDGE,"E23.1.0.0")])],"isStart":true}),makeQuery(id+"F7.opExtrude","CAP_FACE",FACE,{"disambiguationData":[OSD([subQ1,subQ0,sQuery(id+"F6.wireOp",EDGE,"E23.2.0.0")])],"isStart":true}),makeQuery(id+"F7.opExtrude","CAP_FACE",FACE,{"disambiguationData":[OSD([subQ1,subQ0,sQuery(id+"F6.wireOp",EDGE,"E23.3.0.0")])],"isStart":true}),makeQuery(id+"F7.opExtrude","CAP_FACE",FACE,{"disambiguationData":[OSD([subQ1,subQ0,sQuery(id+"F6.wireOp",EDGE,"E23.4.0.0")])],"isStart":true}),makeQuery(id+"F7.opExtrude","CAP_FACE",FACE,{"disambiguationData":[OSD([subQ1,subQ0,sQuery(id+"F6.wireOp",EDGE,"E23.5.0.0")])],"isStart":true}),makeQuery(id+"F7.opExtrude","CAP_FACE",FACE,{"disambiguationData":[OSD([subQ1,subQ0,sQuery(id+"F6.wireOp",EDGE,"E23.6.0.0")])],"isStart":true}),makeQuery(id+"F7.opExtrude","CAP_FACE",FACE,{"disambiguationData":[OSD([subQ1,subQ0,sQuery(id+"F6.wireOp",EDGE,"E23.7.0.0")])],"isStart":true}),makeQuery(id+"F7.opExtrude","CAP_FACE",FACE,{"disambiguationData":[OSD([subQ1,subQ0,sQuery(id+"F6.wireOp",EDGE,"E23.8.0.0")])],"isStart":true}),makeQuery(id+"F7.opExtrude","CAP_FACE",FACE,{"disambiguationData":[OSD([subQ1,subQ0,sQuery(id+"F6.wireOp",EDGE,"E23.9.0.0")])],"isStart":true})]}),makeQuery(id+"F31.opExtrude","SWEPT_FACE",FACE,{"disambiguationData":[OSD([sQuery(id+"F30.wireOp",EDGE,"LmbyR1he-35kO-f53Q-696j-YAIKVnODTwI9")])]}),makeQuery(id+"F31.opExtrude","SWEPT_FACE",FACE,{"disambiguationData":[OSD([sQuery(id+"F30.wireOp",EDGE,"lc0urJVt-xGFD-1UqV-AUzd-Ddt8hkDyLtwQ"),sQuery(id+"F30.wireOp",EDGE,"9e28845e-500e-4894-8802-eb7ad12137a13.MirrorCS")])]}),makeQuery(id+"F31.opExtrude","SWEPT_FACE",FACE,{"disambiguationData":[OSD([sQuery(id+"F30.wireOp",EDGE,"9e28845e-500e-4894-8802-eb7ad12137a10.MirrorCS")])]})]})],"blendedInto":[makeQuery(id+"F31.boolean.opBoolean","MERGE",FACE,{"derivedFrom":[makeQuery(id+"F7.boolean.opBoolean","MERGE",FACE,{"derivedFrom":[makeQuery(id+"F5.boolean.opBoolean","MERGE",FACE,{"derivedFrom":[makeQuery(id+"F3.opExtrude","SWEPT_FACE",FACE,{"disambiguationData":[OSD([subQ1,subQ0])]}),makeQuery(id+"F5.opExtrude","SWEPT_FACE",FACE,{"disambiguationData":[OSD([sQuery(id+"F4.wireOp",EDGE,"QKiYiqoZ-9ux7-oAIY-G16o-4d6qDwNjxzcn")])]}),makeQuery(id+"F5.opExtrude","SWEPT_FACE",FACE,{"disambiguationData":[OSD([sQuery(id+"F4.wireOp",EDGE,"094a8055-67e1-4fbe-9fcd-0e3f748caa500.MirrorCS")])]})]}),makeQuery(id+"F7.opExtrude","CAP_FACE",FACE,{"disambiguationData":[OSD([sQuery(id+"F6.wireOp",EDGE,"E21"),sQuery(id+"F6.wireOp",EDGE,"E22")])],"isStart":true}),makeQuery(id+"F7.opExtrude","CAP_FACE",FACE,{"disambiguationData":[OSD([subQ1,subQ0,sQuery(id+"F6.wireOp",EDGE,"E23.1.0.0")])],"isStart":true}),makeQuery(id+"F7.opExtrude","CAP_FACE",FACE,{"disambiguationData":[OSD([subQ1,subQ0,sQuery(id+"F6.wireOp",EDGE,"E23.2.0.0")])],"isStart":true}),makeQuery(id+"F7.opExtrude","CAP_FACE",FACE,{"disambiguationData":[OSD([subQ1,subQ0,sQuery(id+"F6.wireOp",EDGE,"E23.3.0.0")])],"isStart":true}),makeQuery(id+"F7.opExtrude","CAP_FACE",FACE,{"disambiguationData":[OSD([subQ1,subQ0,sQuery(id+"F6.wireOp",EDGE,"E23.4.0.0")])],"isStart":true}),makeQuery(id+"F7.opExtrude","CAP_FACE",FACE,{"disambiguationData":[OSD([subQ1,subQ0,sQuery(id+"F6.wireOp",EDGE,"E23.5.0.0")])],"isStart":true}),makeQuery(id+"F7.opExtrude","CAP_FACE",FACE,{"disambiguationData":[OSD([subQ1,subQ0,sQuery(id+"F6.wireOp",EDGE,"E23.6.0.0")])],"isStart":true}),makeQuery(id+"F7.opExtrude","CAP_FACE",FACE,{"disambiguationData":[OSD([subQ1,subQ0,sQuery(id+"F6.wireOp",EDGE,"E23.7.0.0")])],"isStart":true}),makeQuery(id+"F7.opExtrude","CAP_FACE",FACE,{"disambiguationData":[OSD([subQ1,subQ0,sQuery(id+"F6.wireOp",EDGE,"E23.8.0.0")])],"isStart":true}),makeQuery(id+"F7.opExtrude","CAP_FACE",FACE,{"disambiguationData":[OSD([subQ1,subQ0,sQuery(id+"F6.wireOp",EDGE,"E23.9.0.0")])],"isStart":true})]}),makeQuery(id+"F31.opExtrude","SWEPT_FACE",FACE,{"disambiguationData":[OSD([sQuery(id+"F30.wireOp",EDGE,"LmbyR1he-35kO-f53Q-696j-YAIKVnODTwI9")])]}),makeQuery(id+"F31.opExtrude","SWEPT_FACE",FACE,{"disambiguationData":[OSD([sQuery(id+"F30.wireOp",EDGE,"lc0urJVt-xGFD-1UqV-AUzd-Ddt8hkDyLtwQ"),sQuery(id+"F30.wireOp",EDGE,"9e28845e-500e-4894-8802-eb7ad12137a13.MirrorCS")])]}),makeQuery(id+"F31.opExtrude","SWEPT_FACE",FACE,{"disambiguationData":[OSD([sQuery(id+"F30.wireOp",EDGE,"9e28845e-500e-4894-8802-eb7ad12137a10.MirrorCS")])]})]})]});}
            var Q10;
            Q10=makeQuery(id+"F31.boolean.opBoolean","MERGE",EDGE,{"derivedFrom":[makeQuery(id+"F5.boolean.opBoolean","MERGE",EDGE,{"derivedFrom":[makeQuery(id+"F3.opExtrude","SWEPT_EDGE",EDGE,{"disambiguationData":[OSD([sQuery(id+"F2.wireOp",EDGE,"E1"),sQuery(id+"F2.wireOp",EDGE,"auNxbXKF-pK2V-sqXS-c08M-DIaJRCpJJF02")])]}),makeQuery(id+"F5.opExtrude","SWEPT_EDGE",EDGE,{"disambiguationData":[OSD([sQuery(id+"F4.wireOp",EDGE,"E6"),sQuery(id+"F4.wireOp",EDGE,"QKiYiqoZ-9ux7-oAIY-G16o-4d6qDwNjxzcn")])]})]}),makeQuery(id+"F31.opExtrude","SWEPT_EDGE",EDGE,{"disambiguationData":[OSD([sQuery(id+"F30.wireOp",EDGE,"E76"),sQuery(id+"F30.wireOp",EDGE,"LmbyR1he-35kO-f53Q-696j-YAIKVnODTwI9")])]})]});
            var Q11;
            Q11=makeQuery(id+"F5.opExtrude","CAP_EDGE",EDGE,{"disambiguationData":[OSD([sQuery(id+"F4.wireOp",EDGE,"QKiYiqoZ-9ux7-oAIY-G16o-4d6qDwNjxzcn")])],"isStart":false});
            var Q12;
            Q12=makeQuery(id+"F5.opExtrude","SWEPT_EDGE",EDGE,{"disambiguationData":[OSD([sQuery(id+"F2.wireOp",EDGE,"auNxbXKF-pK2V-sqXS-c08M-DIaJRCpJJF02"),sQuery(id+"F2.wireOp",EDGE,"bd82aa62-3da5-4588-8fb8-dd676fb609a00.MirrorCS"),sQuery(id+"F4.wireOp",EDGE,"pZRC63if-MIhk-IA8v-DNlQ-6x2yv20jE8mF"),sQuery(id+"F4.wireOp",EDGE,"QKiYiqoZ-9ux7-oAIY-G16o-4d6qDwNjxzcn")])]});
            var Q13;
            {var subQ0=sQuery(id+"F2.wireOp",EDGE,"bd82aa62-3da5-4588-8fb8-dd676fb609a00.MirrorCS");var subQ1=sQuery(id+"F2.wireOp",EDGE,"auNxbXKF-pK2V-sqXS-c08M-DIaJRCpJJF02");Q13=makeQuery(id+"F33.opChamfer","BLEND_EDGE",EDGE,{"blendedFrom":[makeQuery(id+"F31.opExtrude","CAP_EDGE",EDGE,{"disambiguationData":[OSD([sQuery(id+"F30.wireOp",EDGE,"E78.MirrorCS")])],"isStart":false}),makeQuery(id+"F31.boolean.opBoolean","MERGE",FACE,{"derivedFrom":[makeQuery(id+"F7.boolean.opBoolean","MERGE",FACE,{"derivedFrom":[makeQuery(id+"F5.boolean.opBoolean","MERGE",FACE,{"derivedFrom":[makeQuery(id+"F3.opExtrude","SWEPT_FACE",FACE,{"disambiguationData":[OSD([subQ1,subQ0])]}),makeQuery(id+"F5.opExtrude","SWEPT_FACE",FACE,{"disambiguationData":[OSD([sQuery(id+"F4.wireOp",EDGE,"QKiYiqoZ-9ux7-oAIY-G16o-4d6qDwNjxzcn")])]}),makeQuery(id+"F5.opExtrude","SWEPT_FACE",FACE,{"disambiguationData":[OSD([sQuery(id+"F4.wireOp",EDGE,"094a8055-67e1-4fbe-9fcd-0e3f748caa500.MirrorCS")])]})]}),makeQuery(id+"F7.opExtrude","CAP_FACE",FACE,{"disambiguationData":[OSD([sQuery(id+"F6.wireOp",EDGE,"E21"),sQuery(id+"F6.wireOp",EDGE,"E22")])],"isStart":true}),makeQuery(id+"F7.opExtrude","CAP_FACE",FACE,{"disambiguationData":[OSD([subQ1,subQ0,sQuery(id+"F6.wireOp",EDGE,"E23.1.0.0")])],"isStart":true}),makeQuery(id+"F7.opExtrude","CAP_FACE",FACE,{"disambiguationData":[OSD([subQ1,subQ0,sQuery(id+"F6.wireOp",EDGE,"E23.2.0.0")])],"isStart":true}),makeQuery(id+"F7.opExtrude","CAP_FACE",FACE,{"disambiguationData":[OSD([subQ1,subQ0,sQuery(id+"F6.wireOp",EDGE,"E23.3.0.0")])],"isStart":true}),makeQuery(id+"F7.opExtrude","CAP_FACE",FACE,{"disambiguationData":[OSD([subQ1,subQ0,sQuery(id+"F6.wireOp",EDGE,"E23.4.0.0")])],"isStart":true}),makeQuery(id+"F7.opExtrude","CAP_FACE",FACE,{"disambiguationData":[OSD([subQ1,subQ0,sQuery(id+"F6.wireOp",EDGE,"E23.5.0.0")])],"isStart":true}),makeQuery(id+"F7.opExtrude","CAP_FACE",FACE,{"disambiguationData":[OSD([subQ1,subQ0,sQuery(id+"F6.wireOp",EDGE,"E23.6.0.0")])],"isStart":true}),makeQuery(id+"F7.opExtrude","CAP_FACE",FACE,{"disambiguationData":[OSD([subQ1,subQ0,sQuery(id+"F6.wireOp",EDGE,"E23.7.0.0")])],"isStart":true}),makeQuery(id+"F7.opExtrude","CAP_FACE",FACE,{"disambiguationData":[OSD([subQ1,subQ0,sQuery(id+"F6.wireOp",EDGE,"E23.8.0.0")])],"isStart":true}),makeQuery(id+"F7.opExtrude","CAP_FACE",FACE,{"disambiguationData":[OSD([subQ1,subQ0,sQuery(id+"F6.wireOp",EDGE,"E23.9.0.0")])],"isStart":true})]}),makeQuery(id+"F31.opExtrude","SWEPT_FACE",FACE,{"disambiguationData":[OSD([sQuery(id+"F30.wireOp",EDGE,"LmbyR1he-35kO-f53Q-696j-YAIKVnODTwI9")])]}),makeQuery(id+"F31.opExtrude","SWEPT_FACE",FACE,{"disambiguationData":[OSD([sQuery(id+"F30.wireOp",EDGE,"lc0urJVt-xGFD-1UqV-AUzd-Ddt8hkDyLtwQ"),sQuery(id+"F30.wireOp",EDGE,"9e28845e-500e-4894-8802-eb7ad12137a13.MirrorCS")])]}),makeQuery(id+"F31.opExtrude","SWEPT_FACE",FACE,{"disambiguationData":[OSD([sQuery(id+"F30.wireOp",EDGE,"9e28845e-500e-4894-8802-eb7ad12137a10.MirrorCS")])]})]})],"blendedInto":[makeQuery(id+"F31.boolean.opBoolean","MERGE",FACE,{"derivedFrom":[makeQuery(id+"F7.boolean.opBoolean","MERGE",FACE,{"derivedFrom":[makeQuery(id+"F5.boolean.opBoolean","MERGE",FACE,{"derivedFrom":[makeQuery(id+"F3.opExtrude","SWEPT_FACE",FACE,{"disambiguationData":[OSD([subQ1,subQ0])]}),makeQuery(id+"F5.opExtrude","SWEPT_FACE",FACE,{"disambiguationData":[OSD([sQuery(id+"F4.wireOp",EDGE,"QKiYiqoZ-9ux7-oAIY-G16o-4d6qDwNjxzcn")])]}),makeQuery(id+"F5.opExtrude","SWEPT_FACE",FACE,{"disambiguationData":[OSD([sQuery(id+"F4.wireOp",EDGE,"094a8055-67e1-4fbe-9fcd-0e3f748caa500.MirrorCS")])]})]}),makeQuery(id+"F7.opExtrude","CAP_FACE",FACE,{"disambiguationData":[OSD([sQuery(id+"F6.wireOp",EDGE,"E21"),sQuery(id+"F6.wireOp",EDGE,"E22")])],"isStart":true}),makeQuery(id+"F7.opExtrude","CAP_FACE",FACE,{"disambiguationData":[OSD([subQ1,subQ0,sQuery(id+"F6.wireOp",EDGE,"E23.1.0.0")])],"isStart":true}),makeQuery(id+"F7.opExtrude","CAP_FACE",FACE,{"disambiguationData":[OSD([subQ1,subQ0,sQuery(id+"F6.wireOp",EDGE,"E23.2.0.0")])],"isStart":true}),makeQuery(id+"F7.opExtrude","CAP_FACE",FACE,{"disambiguationData":[OSD([subQ1,subQ0,sQuery(id+"F6.wireOp",EDGE,"E23.3.0.0")])],"isStart":true}),makeQuery(id+"F7.opExtrude","CAP_FACE",FACE,{"disambiguationData":[OSD([subQ1,subQ0,sQuery(id+"F6.wireOp",EDGE,"E23.4.0.0")])],"isStart":true}),makeQuery(id+"F7.opExtrude","CAP_FACE",FACE,{"disambiguationData":[OSD([subQ1,subQ0,sQuery(id+"F6.wireOp",EDGE,"E23.5.0.0")])],"isStart":true}),makeQuery(id+"F7.opExtrude","CAP_FACE",FACE,{"disambiguationData":[OSD([subQ1,subQ0,sQuery(id+"F6.wireOp",EDGE,"E23.6.0.0")])],"isStart":true}),makeQuery(id+"F7.opExtrude","CAP_FACE",FACE,{"disambiguationData":[OSD([subQ1,subQ0,sQuery(id+"F6.wireOp",EDGE,"E23.7.0.0")])],"isStart":true}),makeQuery(id+"F7.opExtrude","CAP_FACE",FACE,{"disambiguationData":[OSD([subQ1,subQ0,sQuery(id+"F6.wireOp",EDGE,"E23.8.0.0")])],"isStart":true}),makeQuery(id+"F7.opExtrude","CAP_FACE",FACE,{"disambiguationData":[OSD([subQ1,subQ0,sQuery(id+"F6.wireOp",EDGE,"E23.9.0.0")])],"isStart":true})]}),makeQuery(id+"F31.opExtrude","SWEPT_FACE",FACE,{"disambiguationData":[OSD([sQuery(id+"F30.wireOp",EDGE,"LmbyR1he-35kO-f53Q-696j-YAIKVnODTwI9")])]}),makeQuery(id+"F31.opExtrude","SWEPT_FACE",FACE,{"disambiguationData":[OSD([sQuery(id+"F30.wireOp",EDGE,"lc0urJVt-xGFD-1UqV-AUzd-Ddt8hkDyLtwQ"),sQuery(id+"F30.wireOp",EDGE,"9e28845e-500e-4894-8802-eb7ad12137a13.MirrorCS")])]}),makeQuery(id+"F31.opExtrude","SWEPT_FACE",FACE,{"disambiguationData":[OSD([sQuery(id+"F30.wireOp",EDGE,"9e28845e-500e-4894-8802-eb7ad12137a10.MirrorCS")])]})]})]});}
            var Q14;
            Q14=makeQuery(id+"F31.boolean.opBoolean","MERGE",EDGE,{"derivedFrom":[makeQuery(id+"F5.boolean.opBoolean","MERGE",EDGE,{"derivedFrom":[makeQuery(id+"F3.opExtrude","SWEPT_EDGE",EDGE,{"disambiguationData":[OSD([sQuery(id+"F2.wireOp",EDGE,"E3.MirrorCS"),sQuery(id+"F2.wireOp",EDGE,"bd82aa62-3da5-4588-8fb8-dd676fb609a00.MirrorCS")])]}),makeQuery(id+"F5.opExtrude","SWEPT_EDGE",EDGE,{"disambiguationData":[OSD([sQuery(id+"F4.wireOp",EDGE,"094a8055-67e1-4fbe-9fcd-0e3f748caa500.MirrorCS"),sQuery(id+"F4.wireOp",EDGE,"E7.MirrorCS")])]})]}),makeQuery(id+"F31.opExtrude","SWEPT_EDGE",EDGE,{"disambiguationData":[OSD([sQuery(id+"F30.wireOp",EDGE,"9e28845e-500e-4894-8802-eb7ad12137a10.MirrorCS"),sQuery(id+"F30.wireOp",EDGE,"E78.MirrorCS")])]})]});
            var Q15;
            Q15=makeQuery(id+"F5.opExtrude","CAP_EDGE",EDGE,{"disambiguationData":[OSD([sQuery(id+"F4.wireOp",EDGE,"094a8055-67e1-4fbe-9fcd-0e3f748caa500.MirrorCS")])],"isStart":false});
            var Q16;
            Q16=makeQuery(id+"F5.opExtrude","SWEPT_EDGE",EDGE,{"disambiguationData":[OSD([sQuery(id+"F2.wireOp",EDGE,"auNxbXKF-pK2V-sqXS-c08M-DIaJRCpJJF02"),sQuery(id+"F2.wireOp",EDGE,"bd82aa62-3da5-4588-8fb8-dd676fb609a00.MirrorCS"),sQuery(id+"F4.wireOp",EDGE,"0306e720-a4cd-40da-927f-c33b378fc5130.MirrorCS"),sQuery(id+"F4.wireOp",EDGE,"094a8055-67e1-4fbe-9fcd-0e3f748caa500.MirrorCS")])]});
            var Q17;
            Q17=makeQuery(id+"F5.opExtrude","CAP_EDGE",EDGE,{"disambiguationData":[OSD([sQuery(id+"F4.wireOp",EDGE,"E7.MirrorCS")])],"isStart":false});
            var Q18;
            Q18=makeQuery(id+"F5.opExtrude","CAP_EDGE",EDGE,{"disambiguationData":[OSD([sQuery(id+"F4.wireOp",EDGE,"0306e720-a4cd-40da-927f-c33b378fc5130.MirrorCS")])],"isStart":false});
            var Q19;
            Q19=makeQuery(id+"F5.opExtrude","CAP_EDGE",EDGE,{"disambiguationData":[OSD([sQuery(id+"F4.wireOp",EDGE,"E9")])],"isStart":false});
            var Q20;
            Q20=makeQuery(id+"F5.opExtrude","CAP_EDGE",EDGE,{"disambiguationData":[OSD([sQuery(id+"F4.wireOp",EDGE,"pZRC63if-MIhk-IA8v-DNlQ-6x2yv20jE8mF")])],"isStart":false});
            var Q21;
            {var subQ0=sQuery(id+"F2.wireOp",EDGE,"E2.MirrorCS");var subQ1=sQuery(id+"F2.wireOp",EDGE,"E0");var subQ2=sQuery(id+"F2.wireOp",EDGE,"E3.MirrorCS");Q21=makeQuery(id+"F13.boolean.opBoolean","SPLIT",EDGE,{"disambiguationData":[TD([makeQuery(id+"F3.opExtrude","SWEPT_FACE",FACE,{"disambiguationData":[OSD([subQ2])]})])],"derivedFrom":makeQuery(id+"F3.opExtrude","CAP_EDGE",EDGE,{"disambiguationData":[OSD([subQ1,subQ0])],"isStart":true})});}
            var Q22;
            {var subQ0=sQuery(id+"F2.wireOp",EDGE,"E1");var subQ1=sQuery(id+"F2.wireOp",EDGE,"E2.MirrorCS");var subQ2=sQuery(id+"F2.wireOp",EDGE,"E0");Q22=makeQuery(id+"F13.boolean.opBoolean","SPLIT",EDGE,{"disambiguationData":[TD([makeQuery(id+"F3.opExtrude","SWEPT_FACE",FACE,{"disambiguationData":[OSD([subQ0])]})])],"derivedFrom":makeQuery(id+"F3.opExtrude","CAP_EDGE",EDGE,{"disambiguationData":[OSD([subQ2,subQ1])],"isStart":true})});}
            var Q23;
            Q23=makeQuery(id+"F25.boolean.opBoolean","INTERSECT",EDGE,{"derivedFrom":[makeQuery(id+"F5.opExtrude","SWEPT_FACE",FACE,{"disambiguationData":[OSD([sQuery(id+"F4.wireOp",EDGE,"E9")])]}),makeQuery(id+"F25.opExtrude","SWEPT_FACE",FACE,{"disambiguationData":[OSD([sQuery(id+"F24.wireOp",EDGE,"E65")])]})]});
            var Q24;
            {var subQ0=sQuery(id+"F2.wireOp",EDGE,"bd82aa62-3da5-4588-8fb8-dd676fb609a00.MirrorCS");var subQ1=sQuery(id+"F2.wireOp",EDGE,"auNxbXKF-pK2V-sqXS-c08M-DIaJRCpJJF02");Q24=makeQuery(id+"F33.opChamfer","BLEND_EDGE",EDGE,{"blendedFrom":[makeQuery(id+"F31.opExtrude","CAP_EDGE",EDGE,{"disambiguationData":[OSD([sQuery(id+"F30.wireOp",EDGE,"FnGoxQI1-ApBs-8kJi-dP3M-xmPosOsWHfLG")])],"isStart":false}),makeQuery(id+"F31.boolean.opBoolean","MERGE",FACE,{"derivedFrom":[makeQuery(id+"F7.boolean.opBoolean","MERGE",FACE,{"derivedFrom":[makeQuery(id+"F5.boolean.opBoolean","MERGE",FACE,{"derivedFrom":[makeQuery(id+"F3.opExtrude","SWEPT_FACE",FACE,{"disambiguationData":[OSD([subQ1,subQ0])]}),makeQuery(id+"F5.opExtrude","SWEPT_FACE",FACE,{"disambiguationData":[OSD([sQuery(id+"F4.wireOp",EDGE,"QKiYiqoZ-9ux7-oAIY-G16o-4d6qDwNjxzcn")])]}),makeQuery(id+"F5.opExtrude","SWEPT_FACE",FACE,{"disambiguationData":[OSD([sQuery(id+"F4.wireOp",EDGE,"094a8055-67e1-4fbe-9fcd-0e3f748caa500.MirrorCS")])]})]}),makeQuery(id+"F7.opExtrude","CAP_FACE",FACE,{"disambiguationData":[OSD([sQuery(id+"F6.wireOp",EDGE,"E21"),sQuery(id+"F6.wireOp",EDGE,"E22")])],"isStart":true}),makeQuery(id+"F7.opExtrude","CAP_FACE",FACE,{"disambiguationData":[OSD([subQ1,subQ0,sQuery(id+"F6.wireOp",EDGE,"E23.1.0.0")])],"isStart":true}),makeQuery(id+"F7.opExtrude","CAP_FACE",FACE,{"disambiguationData":[OSD([subQ1,subQ0,sQuery(id+"F6.wireOp",EDGE,"E23.2.0.0")])],"isStart":true}),makeQuery(id+"F7.opExtrude","CAP_FACE",FACE,{"disambiguationData":[OSD([subQ1,subQ0,sQuery(id+"F6.wireOp",EDGE,"E23.3.0.0")])],"isStart":true}),makeQuery(id+"F7.opExtrude","CAP_FACE",FACE,{"disambiguationData":[OSD([subQ1,subQ0,sQuery(id+"F6.wireOp",EDGE,"E23.4.0.0")])],"isStart":true}),makeQuery(id+"F7.opExtrude","CAP_FACE",FACE,{"disambiguationData":[OSD([subQ1,subQ0,sQuery(id+"F6.wireOp",EDGE,"E23.5.0.0")])],"isStart":true}),makeQuery(id+"F7.opExtrude","CAP_FACE",FACE,{"disambiguationData":[OSD([subQ1,subQ0,sQuery(id+"F6.wireOp",EDGE,"E23.6.0.0")])],"isStart":true}),makeQuery(id+"F7.opExtrude","CAP_FACE",FACE,{"disambiguationData":[OSD([subQ1,subQ0,sQuery(id+"F6.wireOp",EDGE,"E23.7.0.0")])],"isStart":true})]}),makeQuery(id+"F31.opExtrude","SWEPT_FACE",FACE,{"disambiguationData":[OSD([sQuery(id+"F30.wireOp",EDGE,"ykEuGFcq-UQF4-khE9-OFNr-bY3PkPlk7WNo")])]}),makeQuery(id+"F31.opExtrude","SWEPT_FACE",FACE,{"disambiguationData":[OSD([sQuery(id+"F30.wireOp",EDGE,"u4Of9TWJ-UFXE-Kmm3-mw3i-iHo4bxCqP4ZF")])]}),makeQuery(id+"F31.opExtrude","SWEPT_FACE",FACE,{"disambiguationData":[OSD([sQuery(id+"F30.wireOp",EDGE,"H6aE8OyH-lJ0U-gGdm-yzXW-P0Mduul7ht97")])]}),makeQuery(id+"F31.opExtrude","SWEPT_FACE",FACE,{"disambiguationData":[OSD([sQuery(id+"F30.wireOp",EDGE,"0taok79N-SHiG-LFBZ-oh4V-C92XCes25FY3")])]})]})],"blendedInto":[makeQuery(id+"F31.boolean.opBoolean","MERGE",FACE,{"derivedFrom":[makeQuery(id+"F7.boolean.opBoolean","MERGE",FACE,{"derivedFrom":[makeQuery(id+"F5.boolean.opBoolean","MERGE",FACE,{"derivedFrom":[makeQuery(id+"F3.opExtrude","SWEPT_FACE",FACE,{"disambiguationData":[OSD([subQ1,subQ0])]}),makeQuery(id+"F5.opExtrude","SWEPT_FACE",FACE,{"disambiguationData":[OSD([sQuery(id+"F4.wireOp",EDGE,"QKiYiqoZ-9ux7-oAIY-G16o-4d6qDwNjxzcn")])]}),makeQuery(id+"F5.opExtrude","SWEPT_FACE",FACE,{"disambiguationData":[OSD([sQuery(id+"F4.wireOp",EDGE,"094a8055-67e1-4fbe-9fcd-0e3f748caa500.MirrorCS")])]})]}),makeQuery(id+"F7.opExtrude","CAP_FACE",FACE,{"disambiguationData":[OSD([sQuery(id+"F6.wireOp",EDGE,"E21"),sQuery(id+"F6.wireOp",EDGE,"E22")])],"isStart":true}),makeQuery(id+"F7.opExtrude","CAP_FACE",FACE,{"disambiguationData":[OSD([subQ1,subQ0,sQuery(id+"F6.wireOp",EDGE,"E23.1.0.0")])],"isStart":true}),makeQuery(id+"F7.opExtrude","CAP_FACE",FACE,{"disambiguationData":[OSD([subQ1,subQ0,sQuery(id+"F6.wireOp",EDGE,"E23.2.0.0")])],"isStart":true}),makeQuery(id+"F7.opExtrude","CAP_FACE",FACE,{"disambiguationData":[OSD([subQ1,subQ0,sQuery(id+"F6.wireOp",EDGE,"E23.3.0.0")])],"isStart":true}),makeQuery(id+"F7.opExtrude","CAP_FACE",FACE,{"disambiguationData":[OSD([subQ1,subQ0,sQuery(id+"F6.wireOp",EDGE,"E23.4.0.0")])],"isStart":true}),makeQuery(id+"F7.opExtrude","CAP_FACE",FACE,{"disambiguationData":[OSD([subQ1,subQ0,sQuery(id+"F6.wireOp",EDGE,"E23.5.0.0")])],"isStart":true}),makeQuery(id+"F7.opExtrude","CAP_FACE",FACE,{"disambiguationData":[OSD([subQ1,subQ0,sQuery(id+"F6.wireOp",EDGE,"E23.6.0.0")])],"isStart":true}),makeQuery(id+"F7.opExtrude","CAP_FACE",FACE,{"disambiguationData":[OSD([subQ1,subQ0,sQuery(id+"F6.wireOp",EDGE,"E23.7.0.0")])],"isStart":true})]}),makeQuery(id+"F31.opExtrude","SWEPT_FACE",FACE,{"disambiguationData":[OSD([sQuery(id+"F30.wireOp",EDGE,"ykEuGFcq-UQF4-khE9-OFNr-bY3PkPlk7WNo")])]}),makeQuery(id+"F31.opExtrude","SWEPT_FACE",FACE,{"disambiguationData":[OSD([sQuery(id+"F30.wireOp",EDGE,"u4Of9TWJ-UFXE-Kmm3-mw3i-iHo4bxCqP4ZF")])]}),makeQuery(id+"F31.opExtrude","SWEPT_FACE",FACE,{"disambiguationData":[OSD([sQuery(id+"F30.wireOp",EDGE,"H6aE8OyH-lJ0U-gGdm-yzXW-P0Mduul7ht97")])]}),makeQuery(id+"F31.opExtrude","SWEPT_FACE",FACE,{"disambiguationData":[OSD([sQuery(id+"F30.wireOp",EDGE,"0taok79N-SHiG-LFBZ-oh4V-C92XCes25FY3")])]})]})]});}
            var Q25;
            {var subQ0=sQuery(id+"F2.wireOp",EDGE,"bd82aa62-3da5-4588-8fb8-dd676fb609a00.MirrorCS");var subQ1=sQuery(id+"F2.wireOp",EDGE,"auNxbXKF-pK2V-sqXS-c08M-DIaJRCpJJF02");Q25=makeQuery(id+"F31.boolean.opBoolean","SPLIT",EDGE,{"disambiguationData":[TD([makeQuery(id+"F31.opExtrude","SWEPT_FACE",FACE,{"disambiguationData":[OSD([sQuery(id+"F30.wireOp",EDGE,"EWeeRF0Z-AfAX-n7vc-ByC2-pyatoFBhdQdW")])]})])],"derivedFrom":makeQuery(id+"F3.opExtrude","CAP_EDGE",EDGE,{"disambiguationData":[OSD([subQ1,subQ0])],"isStart":true})});}
            var Q26;
            {var subQ0=sQuery(id+"F2.wireOp",EDGE,"bd82aa62-3da5-4588-8fb8-dd676fb609a00.MirrorCS");var subQ1=sQuery(id+"F2.wireOp",EDGE,"auNxbXKF-pK2V-sqXS-c08M-DIaJRCpJJF02");Q26=makeQuery(id+"F33.opChamfer","BLEND_EDGE",EDGE,{"blendedFrom":[makeQuery(id+"F31.opExtrude","CAP_EDGE",EDGE,{"disambiguationData":[OSD([sQuery(id+"F30.wireOp",EDGE,"EWeeRF0Z-AfAX-n7vc-ByC2-pyatoFBhdQdW")])],"isStart":false}),makeQuery(id+"F31.boolean.opBoolean","MERGE",FACE,{"derivedFrom":[makeQuery(id+"F7.boolean.opBoolean","MERGE",FACE,{"derivedFrom":[makeQuery(id+"F5.boolean.opBoolean","MERGE",FACE,{"derivedFrom":[makeQuery(id+"F3.opExtrude","SWEPT_FACE",FACE,{"disambiguationData":[OSD([subQ1,subQ0])]}),makeQuery(id+"F5.opExtrude","SWEPT_FACE",FACE,{"disambiguationData":[OSD([sQuery(id+"F4.wireOp",EDGE,"QKiYiqoZ-9ux7-oAIY-G16o-4d6qDwNjxzcn")])]}),makeQuery(id+"F5.opExtrude","SWEPT_FACE",FACE,{"disambiguationData":[OSD([sQuery(id+"F4.wireOp",EDGE,"094a8055-67e1-4fbe-9fcd-0e3f748caa500.MirrorCS")])]})]}),makeQuery(id+"F7.opExtrude","CAP_FACE",FACE,{"disambiguationData":[OSD([sQuery(id+"F6.wireOp",EDGE,"E21"),sQuery(id+"F6.wireOp",EDGE,"E22")])],"isStart":true}),makeQuery(id+"F7.opExtrude","CAP_FACE",FACE,{"disambiguationData":[OSD([subQ1,subQ0,sQuery(id+"F6.wireOp",EDGE,"E23.1.0.0")])],"isStart":true}),makeQuery(id+"F7.opExtrude","CAP_FACE",FACE,{"disambiguationData":[OSD([subQ1,subQ0,sQuery(id+"F6.wireOp",EDGE,"E23.2.0.0")])],"isStart":true}),makeQuery(id+"F7.opExtrude","CAP_FACE",FACE,{"disambiguationData":[OSD([subQ1,subQ0,sQuery(id+"F6.wireOp",EDGE,"E23.3.0.0")])],"isStart":true}),makeQuery(id+"F7.opExtrude","CAP_FACE",FACE,{"disambiguationData":[OSD([subQ1,subQ0,sQuery(id+"F6.wireOp",EDGE,"E23.4.0.0")])],"isStart":true}),makeQuery(id+"F7.opExtrude","CAP_FACE",FACE,{"disambiguationData":[OSD([subQ1,subQ0,sQuery(id+"F6.wireOp",EDGE,"E23.5.0.0")])],"isStart":true}),makeQuery(id+"F7.opExtrude","CAP_FACE",FACE,{"disambiguationData":[OSD([subQ1,subQ0,sQuery(id+"F6.wireOp",EDGE,"E23.6.0.0")])],"isStart":true}),makeQuery(id+"F7.opExtrude","CAP_FACE",FACE,{"disambiguationData":[OSD([subQ1,subQ0,sQuery(id+"F6.wireOp",EDGE,"E23.7.0.0")])],"isStart":true})]}),makeQuery(id+"F31.opExtrude","SWEPT_FACE",FACE,{"disambiguationData":[OSD([sQuery(id+"F30.wireOp",EDGE,"ykEuGFcq-UQF4-khE9-OFNr-bY3PkPlk7WNo")])]}),makeQuery(id+"F31.opExtrude","SWEPT_FACE",FACE,{"disambiguationData":[OSD([sQuery(id+"F30.wireOp",EDGE,"u4Of9TWJ-UFXE-Kmm3-mw3i-iHo4bxCqP4ZF")])]}),makeQuery(id+"F31.opExtrude","SWEPT_FACE",FACE,{"disambiguationData":[OSD([sQuery(id+"F30.wireOp",EDGE,"H6aE8OyH-lJ0U-gGdm-yzXW-P0Mduul7ht97")])]}),makeQuery(id+"F31.opExtrude","SWEPT_FACE",FACE,{"disambiguationData":[OSD([sQuery(id+"F30.wireOp",EDGE,"0taok79N-SHiG-LFBZ-oh4V-C92XCes25FY3")])]})]})],"blendedInto":[makeQuery(id+"F31.boolean.opBoolean","MERGE",FACE,{"derivedFrom":[makeQuery(id+"F7.boolean.opBoolean","MERGE",FACE,{"derivedFrom":[makeQuery(id+"F5.boolean.opBoolean","MERGE",FACE,{"derivedFrom":[makeQuery(id+"F3.opExtrude","SWEPT_FACE",FACE,{"disambiguationData":[OSD([subQ1,subQ0])]}),makeQuery(id+"F5.opExtrude","SWEPT_FACE",FACE,{"disambiguationData":[OSD([sQuery(id+"F4.wireOp",EDGE,"QKiYiqoZ-9ux7-oAIY-G16o-4d6qDwNjxzcn")])]}),makeQuery(id+"F5.opExtrude","SWEPT_FACE",FACE,{"disambiguationData":[OSD([sQuery(id+"F4.wireOp",EDGE,"094a8055-67e1-4fbe-9fcd-0e3f748caa500.MirrorCS")])]})]}),makeQuery(id+"F7.opExtrude","CAP_FACE",FACE,{"disambiguationData":[OSD([sQuery(id+"F6.wireOp",EDGE,"E21"),sQuery(id+"F6.wireOp",EDGE,"E22")])],"isStart":true}),makeQuery(id+"F7.opExtrude","CAP_FACE",FACE,{"disambiguationData":[OSD([subQ1,subQ0,sQuery(id+"F6.wireOp",EDGE,"E23.1.0.0")])],"isStart":true}),makeQuery(id+"F7.opExtrude","CAP_FACE",FACE,{"disambiguationData":[OSD([subQ1,subQ0,sQuery(id+"F6.wireOp",EDGE,"E23.2.0.0")])],"isStart":true}),makeQuery(id+"F7.opExtrude","CAP_FACE",FACE,{"disambiguationData":[OSD([subQ1,subQ0,sQuery(id+"F6.wireOp",EDGE,"E23.3.0.0")])],"isStart":true}),makeQuery(id+"F7.opExtrude","CAP_FACE",FACE,{"disambiguationData":[OSD([subQ1,subQ0,sQuery(id+"F6.wireOp",EDGE,"E23.4.0.0")])],"isStart":true}),makeQuery(id+"F7.opExtrude","CAP_FACE",FACE,{"disambiguationData":[OSD([subQ1,subQ0,sQuery(id+"F6.wireOp",EDGE,"E23.5.0.0")])],"isStart":true}),makeQuery(id+"F7.opExtrude","CAP_FACE",FACE,{"disambiguationData":[OSD([subQ1,subQ0,sQuery(id+"F6.wireOp",EDGE,"E23.6.0.0")])],"isStart":true}),makeQuery(id+"F7.opExtrude","CAP_FACE",FACE,{"disambiguationData":[OSD([subQ1,subQ0,sQuery(id+"F6.wireOp",EDGE,"E23.7.0.0")])],"isStart":true})]}),makeQuery(id+"F31.opExtrude","SWEPT_FACE",FACE,{"disambiguationData":[OSD([sQuery(id+"F30.wireOp",EDGE,"ykEuGFcq-UQF4-khE9-OFNr-bY3PkPlk7WNo")])]}),makeQuery(id+"F31.opExtrude","SWEPT_FACE",FACE,{"disambiguationData":[OSD([sQuery(id+"F30.wireOp",EDGE,"u4Of9TWJ-UFXE-Kmm3-mw3i-iHo4bxCqP4ZF")])]}),makeQuery(id+"F31.opExtrude","SWEPT_FACE",FACE,{"disambiguationData":[OSD([sQuery(id+"F30.wireOp",EDGE,"H6aE8OyH-lJ0U-gGdm-yzXW-P0Mduul7ht97")])]}),makeQuery(id+"F31.opExtrude","SWEPT_FACE",FACE,{"disambiguationData":[OSD([sQuery(id+"F30.wireOp",EDGE,"0taok79N-SHiG-LFBZ-oh4V-C92XCes25FY3")])]})]})]});}
            var Q27;
            Q27=makeQuery(id+"F31.opExtrude","CAP_EDGE",EDGE,{"disambiguationData":[OSD([sQuery(id+"F30.wireOp",EDGE,"H6aE8OyH-lJ0U-gGdm-yzXW-P0Mduul7ht97")])],"isStart":false});
            var Q28;
            Q28=makeQuery(id+"F31.opExtrude","CAP_EDGE",EDGE,{"disambiguationData":[OSD([sQuery(id+"F30.wireOp",EDGE,"0taok79N-SHiG-LFBZ-oh4V-C92XCes25FY3")])],"isStart":false});
            chamfer(context, id + "F34", {"entities" : qUnion([Q0, Q1, Q2, Q3, Q4, Q5, Q6, Q7, Q8, Q9, Q10, Q11, Q12, Q13, Q14, Q15, Q16, Q17, Q18, Q19, Q20, Q21, Q22, Q23, Q24, Q25, Q26, Q27, Q28]), "width" : 1 * mm, "tangentPropagation" : true});
        }
        {
            var Q0;
            Q0=makeQuery(id+"F5.opExtrude","SWEPT_EDGE",EDGE,{"disambiguationData":[OSD([sQuery(id+"F4.wireOp",EDGE,"pZRC63if-MIhk-IA8v-DNlQ-6x2yv20jE8mF"),sQuery(id+"F4.wireOp",EDGE,"E9")])]});
            var Q1;
            Q1=makeQuery(id+"F5.opExtrude","SWEPT_EDGE",EDGE,{"disambiguationData":[OSD([sQuery(id+"F4.wireOp",EDGE,"0306e720-a4cd-40da-927f-c33b378fc5130.MirrorCS"),sQuery(id+"F4.wireOp",EDGE,"E9")])]});
            fillet(context, id + "F35", {"entities" : qUnion([Q0, Q1]), "radius" : 5 * mm, "tangentPropagation" : true, "allowEdgeOverflow" : false});
        }
        {
            var Q0;
            Q0=makeQuery(id+"F31.opExtrude","CAP_EDGE",EDGE,{"disambiguationData":[OSD([sQuery(id+"F30.wireOp",EDGE,"E91")])],"isStart":false});
            var Q1;
            {var subQ0=sQuery(id+"F2.wireOp",EDGE,"E4.top");Q1=makeQuery(id+"F33.opChamfer","BLEND_EDGE",EDGE,{"blendedFrom":[makeQuery(id+"F31.opExtrude","CAP_EDGE",EDGE,{"disambiguationData":[OSD([sQuery(id+"F30.wireOp",EDGE,"E90")])],"isStart":false}),makeQuery(id+"F31.boolean.opBoolean","MERGE",FACE,{"derivedFrom":[makeQuery(id+"F7.boolean.opBoolean","MERGE",FACE,{"derivedFrom":[makeQuery(id+"F5.boolean.opBoolean","MERGE",FACE,{"derivedFrom":[makeQuery(id+"F3.opExtrude","SWEPT_FACE",FACE,{"disambiguationData":[OSD([subQ0])]}),makeQuery(id+"F5.opExtrude","SWEPT_FACE",FACE,{"disambiguationData":[OSD([sQuery(id+"F4.wireOp",EDGE,"E16")])]}),makeQuery(id+"F5.opExtrude","SWEPT_FACE",FACE,{"disambiguationData":[OSD([sQuery(id+"F4.wireOp",EDGE,"E19")])]})]}),makeQuery(id+"F7.opExtrude","CAP_FACE",FACE,{"disambiguationData":[OSD([sQuery(id+"F6.wireOp",EDGE,"E21"),sQuery(id+"F6.wireOp",EDGE,"E22")])],"isStart":true}),makeQuery(id+"F7.opExtrude","CAP_FACE",FACE,{"disambiguationData":[OSD([subQ0,sQuery(id+"F6.wireOp",EDGE,"E23.1.0.0")])],"isStart":true}),makeQuery(id+"F7.opExtrude","CAP_FACE",FACE,{"disambiguationData":[OSD([subQ0,sQuery(id+"F6.wireOp",EDGE,"E23.2.0.0")])],"isStart":true}),makeQuery(id+"F7.opExtrude","CAP_FACE",FACE,{"disambiguationData":[OSD([subQ0,sQuery(id+"F6.wireOp",EDGE,"E23.3.0.0")])],"isStart":true}),makeQuery(id+"F7.opExtrude","CAP_FACE",FACE,{"disambiguationData":[OSD([subQ0,sQuery(id+"F6.wireOp",EDGE,"E23.4.0.0")])],"isStart":true}),makeQuery(id+"F7.opExtrude","CAP_FACE",FACE,{"disambiguationData":[OSD([subQ0,sQuery(id+"F6.wireOp",EDGE,"E23.5.0.0")])],"isStart":true}),makeQuery(id+"F7.opExtrude","CAP_FACE",FACE,{"disambiguationData":[OSD([subQ0,sQuery(id+"F6.wireOp",EDGE,"E23.6.0.0")])],"isStart":true}),makeQuery(id+"F7.opExtrude","CAP_FACE",FACE,{"disambiguationData":[OSD([subQ0,sQuery(id+"F6.wireOp",EDGE,"E23.7.0.0")])],"isStart":true})]}),makeQuery(id+"F31.opExtrude","SWEPT_FACE",FACE,{"disambiguationData":[OSD([sQuery(id+"F30.wireOp",EDGE,"E87")])]}),makeQuery(id+"F31.opExtrude","SWEPT_FACE",FACE,{"disambiguationData":[OSD([sQuery(id+"F30.wireOp",EDGE,"E89")])]}),makeQuery(id+"F31.opExtrude","SWEPT_FACE",FACE,{"disambiguationData":[OSD([sQuery(id+"F30.wireOp",EDGE,"E91")])]})]})],"blendedInto":[makeQuery(id+"F31.boolean.opBoolean","MERGE",FACE,{"derivedFrom":[makeQuery(id+"F7.boolean.opBoolean","MERGE",FACE,{"derivedFrom":[makeQuery(id+"F5.boolean.opBoolean","MERGE",FACE,{"derivedFrom":[makeQuery(id+"F3.opExtrude","SWEPT_FACE",FACE,{"disambiguationData":[OSD([subQ0])]}),makeQuery(id+"F5.opExtrude","SWEPT_FACE",FACE,{"disambiguationData":[OSD([sQuery(id+"F4.wireOp",EDGE,"E16")])]}),makeQuery(id+"F5.opExtrude","SWEPT_FACE",FACE,{"disambiguationData":[OSD([sQuery(id+"F4.wireOp",EDGE,"E19")])]})]}),makeQuery(id+"F7.opExtrude","CAP_FACE",FACE,{"disambiguationData":[OSD([sQuery(id+"F6.wireOp",EDGE,"E21"),sQuery(id+"F6.wireOp",EDGE,"E22")])],"isStart":true}),makeQuery(id+"F7.opExtrude","CAP_FACE",FACE,{"disambiguationData":[OSD([subQ0,sQuery(id+"F6.wireOp",EDGE,"E23.1.0.0")])],"isStart":true}),makeQuery(id+"F7.opExtrude","CAP_FACE",FACE,{"disambiguationData":[OSD([subQ0,sQuery(id+"F6.wireOp",EDGE,"E23.2.0.0")])],"isStart":true}),makeQuery(id+"F7.opExtrude","CAP_FACE",FACE,{"disambiguationData":[OSD([subQ0,sQuery(id+"F6.wireOp",EDGE,"E23.3.0.0")])],"isStart":true}),makeQuery(id+"F7.opExtrude","CAP_FACE",FACE,{"disambiguationData":[OSD([subQ0,sQuery(id+"F6.wireOp",EDGE,"E23.4.0.0")])],"isStart":true}),makeQuery(id+"F7.opExtrude","CAP_FACE",FACE,{"disambiguationData":[OSD([subQ0,sQuery(id+"F6.wireOp",EDGE,"E23.5.0.0")])],"isStart":true}),makeQuery(id+"F7.opExtrude","CAP_FACE",FACE,{"disambiguationData":[OSD([subQ0,sQuery(id+"F6.wireOp",EDGE,"E23.6.0.0")])],"isStart":true}),makeQuery(id+"F7.opExtrude","CAP_FACE",FACE,{"disambiguationData":[OSD([subQ0,sQuery(id+"F6.wireOp",EDGE,"E23.7.0.0")])],"isStart":true})]}),makeQuery(id+"F31.opExtrude","SWEPT_FACE",FACE,{"disambiguationData":[OSD([sQuery(id+"F30.wireOp",EDGE,"E87")])]}),makeQuery(id+"F31.opExtrude","SWEPT_FACE",FACE,{"disambiguationData":[OSD([sQuery(id+"F30.wireOp",EDGE,"E89")])]}),makeQuery(id+"F31.opExtrude","SWEPT_FACE",FACE,{"disambiguationData":[OSD([sQuery(id+"F30.wireOp",EDGE,"E91")])]})]})]});}
            var Q2;
            {var subQ0=sQuery(id+"F2.wireOp",EDGE,"E4.top");Q2=makeQuery(id+"F31.boolean.opBoolean","SPLIT",EDGE,{"disambiguationData":[TD([makeQuery(id+"F31.opExtrude","SWEPT_FACE",FACE,{"disambiguationData":[OSD([sQuery(id+"F30.wireOp",EDGE,"E80")])]})])],"derivedFrom":makeQuery(id+"F3.opExtrude","CAP_EDGE",EDGE,{"disambiguationData":[OSD([subQ0])],"isStart":true})});}
            var Q3;
            {var subQ0=sQuery(id+"F2.wireOp",EDGE,"E4.top");var subQ1=makeQuery(id+"F31.boolean.opBoolean","MERGE",FACE,{"derivedFrom":[makeQuery(id+"F7.boolean.opBoolean","MERGE",FACE,{"derivedFrom":[makeQuery(id+"F5.boolean.opBoolean","MERGE",FACE,{"derivedFrom":[makeQuery(id+"F3.opExtrude","SWEPT_FACE",FACE,{"disambiguationData":[OSD([subQ0])]}),makeQuery(id+"F5.opExtrude","SWEPT_FACE",FACE,{"disambiguationData":[OSD([sQuery(id+"F4.wireOp",EDGE,"E16")])]}),makeQuery(id+"F5.opExtrude","SWEPT_FACE",FACE,{"disambiguationData":[OSD([sQuery(id+"F4.wireOp",EDGE,"E19")])]})]}),makeQuery(id+"F7.opExtrude","CAP_FACE",FACE,{"disambiguationData":[OSD([sQuery(id+"F6.wireOp",EDGE,"E21"),sQuery(id+"F6.wireOp",EDGE,"E22")])],"isStart":true}),makeQuery(id+"F7.opExtrude","CAP_FACE",FACE,{"disambiguationData":[OSD([subQ0,sQuery(id+"F6.wireOp",EDGE,"E23.1.0.0")])],"isStart":true}),makeQuery(id+"F7.opExtrude","CAP_FACE",FACE,{"disambiguationData":[OSD([subQ0,sQuery(id+"F6.wireOp",EDGE,"E23.2.0.0")])],"isStart":true}),makeQuery(id+"F7.opExtrude","CAP_FACE",FACE,{"disambiguationData":[OSD([subQ0,sQuery(id+"F6.wireOp",EDGE,"E23.3.0.0")])],"isStart":true}),makeQuery(id+"F7.opExtrude","CAP_FACE",FACE,{"disambiguationData":[OSD([subQ0,sQuery(id+"F6.wireOp",EDGE,"E23.4.0.0")])],"isStart":true}),makeQuery(id+"F7.opExtrude","CAP_FACE",FACE,{"disambiguationData":[OSD([subQ0,sQuery(id+"F6.wireOp",EDGE,"E23.5.0.0")])],"isStart":true}),makeQuery(id+"F7.opExtrude","CAP_FACE",FACE,{"disambiguationData":[OSD([subQ0,sQuery(id+"F6.wireOp",EDGE,"E23.6.0.0")])],"isStart":true}),makeQuery(id+"F7.opExtrude","CAP_FACE",FACE,{"disambiguationData":[OSD([subQ0,sQuery(id+"F6.wireOp",EDGE,"E23.7.0.0")])],"isStart":true})]}),makeQuery(id+"F31.opExtrude","SWEPT_FACE",FACE,{"disambiguationData":[OSD([sQuery(id+"F30.wireOp",EDGE,"E87")])]}),makeQuery(id+"F31.opExtrude","SWEPT_FACE",FACE,{"disambiguationData":[OSD([sQuery(id+"F30.wireOp",EDGE,"E89")])]}),makeQuery(id+"F31.opExtrude","SWEPT_FACE",FACE,{"disambiguationData":[OSD([sQuery(id+"F30.wireOp",EDGE,"E91")])]})]});Q3=makeQuery(id+"F34.opChamfer","BLEND_EDGE",EDGE,{"blendedFrom":[makeQuery(id+"F33.opChamfer","BLEND_EDGE",EDGE,{"blendedFrom":[makeQuery(id+"F31.opExtrude","CAP_EDGE",EDGE,{"disambiguationData":[OSD([sQuery(id+"F30.wireOp",EDGE,"E80")])],"isStart":false}),subQ1],"blendedInto":[subQ1]}),subQ1],"blendedInto":[subQ1]});}
            var Q4;
            Q4=makeQuery(id+"F31.opExtrude","CAP_EDGE",EDGE,{"disambiguationData":[OSD([sQuery(id+"F30.wireOp",EDGE,"E87")])],"isStart":false});
            var Q5;
            {var subQ0=sQuery(id+"F2.wireOp",EDGE,"E4.top");Q5=makeQuery(id+"F33.opChamfer","BLEND_EDGE",EDGE,{"blendedFrom":[makeQuery(id+"F31.opExtrude","CAP_EDGE",EDGE,{"disambiguationData":[OSD([sQuery(id+"F30.wireOp",EDGE,"E88")])],"isStart":false}),makeQuery(id+"F31.boolean.opBoolean","MERGE",FACE,{"derivedFrom":[makeQuery(id+"F7.boolean.opBoolean","MERGE",FACE,{"derivedFrom":[makeQuery(id+"F5.boolean.opBoolean","MERGE",FACE,{"derivedFrom":[makeQuery(id+"F3.opExtrude","SWEPT_FACE",FACE,{"disambiguationData":[OSD([subQ0])]}),makeQuery(id+"F5.opExtrude","SWEPT_FACE",FACE,{"disambiguationData":[OSD([sQuery(id+"F4.wireOp",EDGE,"E16")])]}),makeQuery(id+"F5.opExtrude","SWEPT_FACE",FACE,{"disambiguationData":[OSD([sQuery(id+"F4.wireOp",EDGE,"E19")])]})]}),makeQuery(id+"F7.opExtrude","CAP_FACE",FACE,{"disambiguationData":[OSD([sQuery(id+"F6.wireOp",EDGE,"E21"),sQuery(id+"F6.wireOp",EDGE,"E22")])],"isStart":true}),makeQuery(id+"F7.opExtrude","CAP_FACE",FACE,{"disambiguationData":[OSD([subQ0,sQuery(id+"F6.wireOp",EDGE,"E23.1.0.0")])],"isStart":true}),makeQuery(id+"F7.opExtrude","CAP_FACE",FACE,{"disambiguationData":[OSD([subQ0,sQuery(id+"F6.wireOp",EDGE,"E23.2.0.0")])],"isStart":true}),makeQuery(id+"F7.opExtrude","CAP_FACE",FACE,{"disambiguationData":[OSD([subQ0,sQuery(id+"F6.wireOp",EDGE,"E23.3.0.0")])],"isStart":true}),makeQuery(id+"F7.opExtrude","CAP_FACE",FACE,{"disambiguationData":[OSD([subQ0,sQuery(id+"F6.wireOp",EDGE,"E23.4.0.0")])],"isStart":true}),makeQuery(id+"F7.opExtrude","CAP_FACE",FACE,{"disambiguationData":[OSD([subQ0,sQuery(id+"F6.wireOp",EDGE,"E23.5.0.0")])],"isStart":true}),makeQuery(id+"F7.opExtrude","CAP_FACE",FACE,{"disambiguationData":[OSD([subQ0,sQuery(id+"F6.wireOp",EDGE,"E23.6.0.0")])],"isStart":true}),makeQuery(id+"F7.opExtrude","CAP_FACE",FACE,{"disambiguationData":[OSD([subQ0,sQuery(id+"F6.wireOp",EDGE,"E23.7.0.0")])],"isStart":true})]}),makeQuery(id+"F31.opExtrude","SWEPT_FACE",FACE,{"disambiguationData":[OSD([sQuery(id+"F30.wireOp",EDGE,"E87")])]}),makeQuery(id+"F31.opExtrude","SWEPT_FACE",FACE,{"disambiguationData":[OSD([sQuery(id+"F30.wireOp",EDGE,"E89")])]}),makeQuery(id+"F31.opExtrude","SWEPT_FACE",FACE,{"disambiguationData":[OSD([sQuery(id+"F30.wireOp",EDGE,"E91")])]})]})],"blendedInto":[makeQuery(id+"F31.boolean.opBoolean","MERGE",FACE,{"derivedFrom":[makeQuery(id+"F7.boolean.opBoolean","MERGE",FACE,{"derivedFrom":[makeQuery(id+"F5.boolean.opBoolean","MERGE",FACE,{"derivedFrom":[makeQuery(id+"F3.opExtrude","SWEPT_FACE",FACE,{"disambiguationData":[OSD([subQ0])]}),makeQuery(id+"F5.opExtrude","SWEPT_FACE",FACE,{"disambiguationData":[OSD([sQuery(id+"F4.wireOp",EDGE,"E16")])]}),makeQuery(id+"F5.opExtrude","SWEPT_FACE",FACE,{"disambiguationData":[OSD([sQuery(id+"F4.wireOp",EDGE,"E19")])]})]}),makeQuery(id+"F7.opExtrude","CAP_FACE",FACE,{"disambiguationData":[OSD([sQuery(id+"F6.wireOp",EDGE,"E21"),sQuery(id+"F6.wireOp",EDGE,"E22")])],"isStart":true}),makeQuery(id+"F7.opExtrude","CAP_FACE",FACE,{"disambiguationData":[OSD([subQ0,sQuery(id+"F6.wireOp",EDGE,"E23.1.0.0")])],"isStart":true}),makeQuery(id+"F7.opExtrude","CAP_FACE",FACE,{"disambiguationData":[OSD([subQ0,sQuery(id+"F6.wireOp",EDGE,"E23.2.0.0")])],"isStart":true}),makeQuery(id+"F7.opExtrude","CAP_FACE",FACE,{"disambiguationData":[OSD([subQ0,sQuery(id+"F6.wireOp",EDGE,"E23.3.0.0")])],"isStart":true}),makeQuery(id+"F7.opExtrude","CAP_FACE",FACE,{"disambiguationData":[OSD([subQ0,sQuery(id+"F6.wireOp",EDGE,"E23.4.0.0")])],"isStart":true}),makeQuery(id+"F7.opExtrude","CAP_FACE",FACE,{"disambiguationData":[OSD([subQ0,sQuery(id+"F6.wireOp",EDGE,"E23.5.0.0")])],"isStart":true}),makeQuery(id+"F7.opExtrude","CAP_FACE",FACE,{"disambiguationData":[OSD([subQ0,sQuery(id+"F6.wireOp",EDGE,"E23.6.0.0")])],"isStart":true}),makeQuery(id+"F7.opExtrude","CAP_FACE",FACE,{"disambiguationData":[OSD([subQ0,sQuery(id+"F6.wireOp",EDGE,"E23.7.0.0")])],"isStart":true})]}),makeQuery(id+"F31.opExtrude","SWEPT_FACE",FACE,{"disambiguationData":[OSD([sQuery(id+"F30.wireOp",EDGE,"E87")])]}),makeQuery(id+"F31.opExtrude","SWEPT_FACE",FACE,{"disambiguationData":[OSD([sQuery(id+"F30.wireOp",EDGE,"E89")])]}),makeQuery(id+"F31.opExtrude","SWEPT_FACE",FACE,{"disambiguationData":[OSD([sQuery(id+"F30.wireOp",EDGE,"E91")])]})]})]});}
            var Q6;
            Q6=makeQuery(id+"F31.opExtrude","CAP_EDGE",EDGE,{"disambiguationData":[OSD([sQuery(id+"F30.wireOp",EDGE,"E89")])],"isStart":false});
            var Q7;
            {var subQ0=sQuery(id+"F2.wireOp",EDGE,"E4.top");Q7=makeQuery(id+"F33.opChamfer","BLEND_EDGE",EDGE,{"blendedFrom":[makeQuery(id+"F31.opExtrude","CAP_EDGE",EDGE,{"disambiguationData":[OSD([sQuery(id+"F30.wireOp",EDGE,"E93")])],"isStart":false}),makeQuery(id+"F31.boolean.opBoolean","MERGE",FACE,{"derivedFrom":[makeQuery(id+"F7.boolean.opBoolean","MERGE",FACE,{"derivedFrom":[makeQuery(id+"F5.boolean.opBoolean","MERGE",FACE,{"derivedFrom":[makeQuery(id+"F3.opExtrude","SWEPT_FACE",FACE,{"disambiguationData":[OSD([subQ0])]}),makeQuery(id+"F5.opExtrude","SWEPT_FACE",FACE,{"disambiguationData":[OSD([sQuery(id+"F4.wireOp",EDGE,"E16")])]}),makeQuery(id+"F5.opExtrude","SWEPT_FACE",FACE,{"disambiguationData":[OSD([sQuery(id+"F4.wireOp",EDGE,"E19")])]})]}),makeQuery(id+"F7.opExtrude","CAP_FACE",FACE,{"disambiguationData":[OSD([sQuery(id+"F6.wireOp",EDGE,"E21"),sQuery(id+"F6.wireOp",EDGE,"E22")])],"isStart":true}),makeQuery(id+"F7.opExtrude","CAP_FACE",FACE,{"disambiguationData":[OSD([subQ0,sQuery(id+"F6.wireOp",EDGE,"E23.1.0.0")])],"isStart":true}),makeQuery(id+"F7.opExtrude","CAP_FACE",FACE,{"disambiguationData":[OSD([subQ0,sQuery(id+"F6.wireOp",EDGE,"E23.2.0.0")])],"isStart":true}),makeQuery(id+"F7.opExtrude","CAP_FACE",FACE,{"disambiguationData":[OSD([subQ0,sQuery(id+"F6.wireOp",EDGE,"E23.3.0.0")])],"isStart":true}),makeQuery(id+"F7.opExtrude","CAP_FACE",FACE,{"disambiguationData":[OSD([subQ0,sQuery(id+"F6.wireOp",EDGE,"E23.4.0.0")])],"isStart":true}),makeQuery(id+"F7.opExtrude","CAP_FACE",FACE,{"disambiguationData":[OSD([subQ0,sQuery(id+"F6.wireOp",EDGE,"E23.5.0.0")])],"isStart":true}),makeQuery(id+"F7.opExtrude","CAP_FACE",FACE,{"disambiguationData":[OSD([subQ0,sQuery(id+"F6.wireOp",EDGE,"E23.6.0.0")])],"isStart":true}),makeQuery(id+"F7.opExtrude","CAP_FACE",FACE,{"disambiguationData":[OSD([subQ0,sQuery(id+"F6.wireOp",EDGE,"E23.7.0.0")])],"isStart":true})]}),makeQuery(id+"F31.opExtrude","SWEPT_FACE",FACE,{"disambiguationData":[OSD([sQuery(id+"F30.wireOp",EDGE,"E87")])]}),makeQuery(id+"F31.opExtrude","SWEPT_FACE",FACE,{"disambiguationData":[OSD([sQuery(id+"F30.wireOp",EDGE,"E89")])]}),makeQuery(id+"F31.opExtrude","SWEPT_FACE",FACE,{"disambiguationData":[OSD([sQuery(id+"F30.wireOp",EDGE,"E91")])]})]})],"blendedInto":[makeQuery(id+"F31.boolean.opBoolean","MERGE",FACE,{"derivedFrom":[makeQuery(id+"F7.boolean.opBoolean","MERGE",FACE,{"derivedFrom":[makeQuery(id+"F5.boolean.opBoolean","MERGE",FACE,{"derivedFrom":[makeQuery(id+"F3.opExtrude","SWEPT_FACE",FACE,{"disambiguationData":[OSD([subQ0])]}),makeQuery(id+"F5.opExtrude","SWEPT_FACE",FACE,{"disambiguationData":[OSD([sQuery(id+"F4.wireOp",EDGE,"E16")])]}),makeQuery(id+"F5.opExtrude","SWEPT_FACE",FACE,{"disambiguationData":[OSD([sQuery(id+"F4.wireOp",EDGE,"E19")])]})]}),makeQuery(id+"F7.opExtrude","CAP_FACE",FACE,{"disambiguationData":[OSD([sQuery(id+"F6.wireOp",EDGE,"E21"),sQuery(id+"F6.wireOp",EDGE,"E22")])],"isStart":true}),makeQuery(id+"F7.opExtrude","CAP_FACE",FACE,{"disambiguationData":[OSD([subQ0,sQuery(id+"F6.wireOp",EDGE,"E23.1.0.0")])],"isStart":true}),makeQuery(id+"F7.opExtrude","CAP_FACE",FACE,{"disambiguationData":[OSD([subQ0,sQuery(id+"F6.wireOp",EDGE,"E23.2.0.0")])],"isStart":true}),makeQuery(id+"F7.opExtrude","CAP_FACE",FACE,{"disambiguationData":[OSD([subQ0,sQuery(id+"F6.wireOp",EDGE,"E23.3.0.0")])],"isStart":true}),makeQuery(id+"F7.opExtrude","CAP_FACE",FACE,{"disambiguationData":[OSD([subQ0,sQuery(id+"F6.wireOp",EDGE,"E23.4.0.0")])],"isStart":true}),makeQuery(id+"F7.opExtrude","CAP_FACE",FACE,{"disambiguationData":[OSD([subQ0,sQuery(id+"F6.wireOp",EDGE,"E23.5.0.0")])],"isStart":true}),makeQuery(id+"F7.opExtrude","CAP_FACE",FACE,{"disambiguationData":[OSD([subQ0,sQuery(id+"F6.wireOp",EDGE,"E23.6.0.0")])],"isStart":true}),makeQuery(id+"F7.opExtrude","CAP_FACE",FACE,{"disambiguationData":[OSD([subQ0,sQuery(id+"F6.wireOp",EDGE,"E23.7.0.0")])],"isStart":true})]}),makeQuery(id+"F31.opExtrude","SWEPT_FACE",FACE,{"disambiguationData":[OSD([sQuery(id+"F30.wireOp",EDGE,"E87")])]}),makeQuery(id+"F31.opExtrude","SWEPT_FACE",FACE,{"disambiguationData":[OSD([sQuery(id+"F30.wireOp",EDGE,"E89")])]}),makeQuery(id+"F31.opExtrude","SWEPT_FACE",FACE,{"disambiguationData":[OSD([sQuery(id+"F30.wireOp",EDGE,"E91")])]})]})]});}
            var Q8;
            {var subQ0=sQuery(id+"F2.wireOp",EDGE,"E4.top");Q8=makeQuery(id+"F31.boolean.opBoolean","SPLIT",EDGE,{"disambiguationData":[TD([makeQuery(id+"F31.opExtrude","SWEPT_FACE",FACE,{"disambiguationData":[OSD([sQuery(id+"F30.wireOp",EDGE,"E84.MirrorCS")])]})])],"derivedFrom":makeQuery(id+"F3.opExtrude","CAP_EDGE",EDGE,{"disambiguationData":[OSD([subQ0])],"isStart":true})});}
            var Q9;
            Q9=makeQuery(id+"F31.boolean.opBoolean","MERGE",EDGE,{"derivedFrom":[makeQuery(id+"F5.boolean.opBoolean","MERGE",EDGE,{"derivedFrom":[makeQuery(id+"F3.opExtrude","SWEPT_EDGE",EDGE,{"disambiguationData":[OSD([sQuery(id+"F2.wireOp",EDGE,"E4.top"),sQuery(id+"F2.wireOp",EDGE,"E4.left")])]}),makeQuery(id+"F5.opExtrude","SWEPT_EDGE",EDGE,{"disambiguationData":[OSD([sQuery(id+"F4.wireOp",EDGE,"E15"),sQuery(id+"F4.wireOp",EDGE,"E16")])]})]}),makeQuery(id+"F31.opExtrude","SWEPT_EDGE",EDGE,{"disambiguationData":[OSD([sQuery(id+"F30.wireOp",EDGE,"E89"),sQuery(id+"F30.wireOp",EDGE,"E93")])]})]});
            var Q10;
            {var subQ0=sQuery(id+"F2.wireOp",EDGE,"E4.top");Q10=makeQuery(id+"F33.opChamfer","BLEND_EDGE",EDGE,{"blendedFrom":[makeQuery(id+"F31.opExtrude","CAP_EDGE",EDGE,{"disambiguationData":[OSD([sQuery(id+"F30.wireOp",EDGE,"E92")])],"isStart":false}),makeQuery(id+"F31.boolean.opBoolean","MERGE",FACE,{"derivedFrom":[makeQuery(id+"F7.boolean.opBoolean","MERGE",FACE,{"derivedFrom":[makeQuery(id+"F5.boolean.opBoolean","MERGE",FACE,{"derivedFrom":[makeQuery(id+"F3.opExtrude","SWEPT_FACE",FACE,{"disambiguationData":[OSD([subQ0])]}),makeQuery(id+"F5.opExtrude","SWEPT_FACE",FACE,{"disambiguationData":[OSD([sQuery(id+"F4.wireOp",EDGE,"E16")])]}),makeQuery(id+"F5.opExtrude","SWEPT_FACE",FACE,{"disambiguationData":[OSD([sQuery(id+"F4.wireOp",EDGE,"E19")])]})]}),makeQuery(id+"F7.opExtrude","CAP_FACE",FACE,{"disambiguationData":[OSD([sQuery(id+"F6.wireOp",EDGE,"E21"),sQuery(id+"F6.wireOp",EDGE,"E22")])],"isStart":true}),makeQuery(id+"F7.opExtrude","CAP_FACE",FACE,{"disambiguationData":[OSD([subQ0,sQuery(id+"F6.wireOp",EDGE,"E23.1.0.0")])],"isStart":true}),makeQuery(id+"F7.opExtrude","CAP_FACE",FACE,{"disambiguationData":[OSD([subQ0,sQuery(id+"F6.wireOp",EDGE,"E23.2.0.0")])],"isStart":true}),makeQuery(id+"F7.opExtrude","CAP_FACE",FACE,{"disambiguationData":[OSD([subQ0,sQuery(id+"F6.wireOp",EDGE,"E23.3.0.0")])],"isStart":true}),makeQuery(id+"F7.opExtrude","CAP_FACE",FACE,{"disambiguationData":[OSD([subQ0,sQuery(id+"F6.wireOp",EDGE,"E23.4.0.0")])],"isStart":true}),makeQuery(id+"F7.opExtrude","CAP_FACE",FACE,{"disambiguationData":[OSD([subQ0,sQuery(id+"F6.wireOp",EDGE,"E23.5.0.0")])],"isStart":true}),makeQuery(id+"F7.opExtrude","CAP_FACE",FACE,{"disambiguationData":[OSD([subQ0,sQuery(id+"F6.wireOp",EDGE,"E23.6.0.0")])],"isStart":true}),makeQuery(id+"F7.opExtrude","CAP_FACE",FACE,{"disambiguationData":[OSD([subQ0,sQuery(id+"F6.wireOp",EDGE,"E23.7.0.0")])],"isStart":true})]}),makeQuery(id+"F31.opExtrude","SWEPT_FACE",FACE,{"disambiguationData":[OSD([sQuery(id+"F30.wireOp",EDGE,"E87")])]}),makeQuery(id+"F31.opExtrude","SWEPT_FACE",FACE,{"disambiguationData":[OSD([sQuery(id+"F30.wireOp",EDGE,"E89")])]}),makeQuery(id+"F31.opExtrude","SWEPT_FACE",FACE,{"disambiguationData":[OSD([sQuery(id+"F30.wireOp",EDGE,"E91")])]})]})],"blendedInto":[makeQuery(id+"F31.boolean.opBoolean","MERGE",FACE,{"derivedFrom":[makeQuery(id+"F7.boolean.opBoolean","MERGE",FACE,{"derivedFrom":[makeQuery(id+"F5.boolean.opBoolean","MERGE",FACE,{"derivedFrom":[makeQuery(id+"F3.opExtrude","SWEPT_FACE",FACE,{"disambiguationData":[OSD([subQ0])]}),makeQuery(id+"F5.opExtrude","SWEPT_FACE",FACE,{"disambiguationData":[OSD([sQuery(id+"F4.wireOp",EDGE,"E16")])]}),makeQuery(id+"F5.opExtrude","SWEPT_FACE",FACE,{"disambiguationData":[OSD([sQuery(id+"F4.wireOp",EDGE,"E19")])]})]}),makeQuery(id+"F7.opExtrude","CAP_FACE",FACE,{"disambiguationData":[OSD([sQuery(id+"F6.wireOp",EDGE,"E21"),sQuery(id+"F6.wireOp",EDGE,"E22")])],"isStart":true}),makeQuery(id+"F7.opExtrude","CAP_FACE",FACE,{"disambiguationData":[OSD([subQ0,sQuery(id+"F6.wireOp",EDGE,"E23.1.0.0")])],"isStart":true}),makeQuery(id+"F7.opExtrude","CAP_FACE",FACE,{"disambiguationData":[OSD([subQ0,sQuery(id+"F6.wireOp",EDGE,"E23.2.0.0")])],"isStart":true}),makeQuery(id+"F7.opExtrude","CAP_FACE",FACE,{"disambiguationData":[OSD([subQ0,sQuery(id+"F6.wireOp",EDGE,"E23.3.0.0")])],"isStart":true}),makeQuery(id+"F7.opExtrude","CAP_FACE",FACE,{"disambiguationData":[OSD([subQ0,sQuery(id+"F6.wireOp",EDGE,"E23.4.0.0")])],"isStart":true}),makeQuery(id+"F7.opExtrude","CAP_FACE",FACE,{"disambiguationData":[OSD([subQ0,sQuery(id+"F6.wireOp",EDGE,"E23.5.0.0")])],"isStart":true}),makeQuery(id+"F7.opExtrude","CAP_FACE",FACE,{"disambiguationData":[OSD([subQ0,sQuery(id+"F6.wireOp",EDGE,"E23.6.0.0")])],"isStart":true}),makeQuery(id+"F7.opExtrude","CAP_FACE",FACE,{"disambiguationData":[OSD([subQ0,sQuery(id+"F6.wireOp",EDGE,"E23.7.0.0")])],"isStart":true})]}),makeQuery(id+"F31.opExtrude","SWEPT_FACE",FACE,{"disambiguationData":[OSD([sQuery(id+"F30.wireOp",EDGE,"E87")])]}),makeQuery(id+"F31.opExtrude","SWEPT_FACE",FACE,{"disambiguationData":[OSD([sQuery(id+"F30.wireOp",EDGE,"E89")])]}),makeQuery(id+"F31.opExtrude","SWEPT_FACE",FACE,{"disambiguationData":[OSD([sQuery(id+"F30.wireOp",EDGE,"E91")])]})]})]});}
            var Q11;
            Q11=makeQuery(id+"F31.boolean.opBoolean","MERGE",EDGE,{"derivedFrom":[makeQuery(id+"F5.boolean.opBoolean","MERGE",EDGE,{"derivedFrom":[makeQuery(id+"F3.opExtrude","SWEPT_EDGE",EDGE,{"disambiguationData":[OSD([sQuery(id+"F2.wireOp",EDGE,"E4.top"),sQuery(id+"F2.wireOp",EDGE,"E4.right")])]}),makeQuery(id+"F5.opExtrude","SWEPT_EDGE",EDGE,{"disambiguationData":[OSD([sQuery(id+"F4.wireOp",EDGE,"E19"),sQuery(id+"F4.wireOp",EDGE,"E20")])]})]}),makeQuery(id+"F31.opExtrude","SWEPT_EDGE",EDGE,{"disambiguationData":[OSD([sQuery(id+"F30.wireOp",EDGE,"E91"),sQuery(id+"F30.wireOp",EDGE,"E92")])]})]});
            var Q12;
            Q12=makeQuery(id+"F5.opExtrude","CAP_EDGE",EDGE,{"disambiguationData":[OSD([sQuery(id+"F4.wireOp",EDGE,"E16")])],"isStart":false});
            var Q13;
            Q13=makeQuery(id+"F5.opExtrude","SWEPT_EDGE",EDGE,{"disambiguationData":[OSD([sQuery(id+"F2.wireOp",EDGE,"E4.top"),sQuery(id+"F4.wireOp",EDGE,"E16"),sQuery(id+"F4.wireOp",EDGE,"E17")])]});
            var Q14;
            {var subQ0=sQuery(id+"F2.wireOp",EDGE,"E4.top");var subQ1=sQuery(id+"F6.wireOp",EDGE,"E21");Q14=makeQuery(id+"F7.boolean.opBoolean","SPLIT",EDGE,{"disambiguationData":[TD([makeQuery(id+"F3.opExtrude","CAP_FACE",FACE,{"disambiguationData":[OSD([sQuery(id+"F2.wireOp",EDGE,"E0"),sQuery(id+"F2.wireOp",EDGE,"E1"),sQuery(id+"F2.wireOp",EDGE,"E2.MirrorCS"),sQuery(id+"F2.wireOp",EDGE,"E3.MirrorCS"),subQ0,sQuery(id+"F2.wireOp",EDGE,"E4.left"),sQuery(id+"F2.wireOp",EDGE,"E4.right")])],"isStart":false}),makeQuery(id+"F3.opExtrude","SWEPT_FACE",FACE,{"disambiguationData":[OSD([subQ0])]}),makeQuery(id+"F5.opExtrude","SWEPT_FACE",FACE,{"disambiguationData":[OSD([sQuery(id+"F4.wireOp",EDGE,"E16")])]}),makeQuery(id+"F5.opExtrude","SWEPT_FACE",FACE,{"disambiguationData":[OSD([sQuery(id+"F4.wireOp",EDGE,"E17")])]}),makeQuery(id+"F5.opExtrude","SWEPT_FACE",FACE,{"disambiguationData":[OSD([sQuery(id+"F4.wireOp",EDGE,"E19")])]}),makeQuery(id+"F7.opExtrude","SWEPT_FACE",FACE,{"disambiguationData":[OSD([subQ1])]}),makeQuery(id+"F7.opExtrude","CAP_FACE",FACE,{"disambiguationData":[OSD([subQ1,sQuery(id+"F6.wireOp",EDGE,"E22")])],"isStart":true}),makeQuery(id+"F7.opExtrude","CAP_FACE",FACE,{"disambiguationData":[OSD([subQ0,sQuery(id+"F6.wireOp",EDGE,"E23.1.0.0")])],"isStart":true}),makeQuery(id+"F7.opExtrude","CAP_FACE",FACE,{"disambiguationData":[OSD([subQ0,sQuery(id+"F6.wireOp",EDGE,"E23.2.0.0")])],"isStart":true}),makeQuery(id+"F7.opExtrude","CAP_FACE",FACE,{"disambiguationData":[OSD([subQ0,sQuery(id+"F6.wireOp",EDGE,"E23.3.0.0")])],"isStart":true}),makeQuery(id+"F7.opExtrude","CAP_FACE",FACE,{"disambiguationData":[OSD([subQ0,sQuery(id+"F6.wireOp",EDGE,"E23.4.0.0")])],"isStart":true}),makeQuery(id+"F7.opExtrude","CAP_FACE",FACE,{"disambiguationData":[OSD([subQ0,sQuery(id+"F6.wireOp",EDGE,"E23.5.0.0")])],"isStart":true}),makeQuery(id+"F7.opExtrude","CAP_FACE",FACE,{"disambiguationData":[OSD([subQ0,sQuery(id+"F6.wireOp",EDGE,"E23.6.0.0")])],"isStart":true}),makeQuery(id+"F7.opExtrude","CAP_FACE",FACE,{"disambiguationData":[OSD([subQ0,sQuery(id+"F6.wireOp",EDGE,"E23.7.0.0")])],"isStart":true})])],"derivedFrom":makeQuery(id+"F3.opExtrude","CAP_EDGE",EDGE,{"disambiguationData":[OSD([subQ0])],"isStart":false})});}
            var Q15;
            Q15=makeQuery(id+"F5.opExtrude","SWEPT_EDGE",EDGE,{"disambiguationData":[OSD([sQuery(id+"F2.wireOp",EDGE,"E4.top"),sQuery(id+"F4.wireOp",EDGE,"E18"),sQuery(id+"F4.wireOp",EDGE,"E19")])]});
            var Q16;
            Q16=makeQuery(id+"F5.opExtrude","CAP_EDGE",EDGE,{"disambiguationData":[OSD([sQuery(id+"F4.wireOp",EDGE,"E19")])],"isStart":false});
            chamfer(context, id + "F36", {"entities" : qUnion([Q0, Q1, Q2, Q3, Q4, Q5, Q6, Q7, Q8, Q9, Q10, Q11, Q12, Q13, Q14, Q15, Q16]), "width" : 1 * mm, "tangentPropagation" : true});
        }
        {
            var Q0;
            Q0=makeQuery(id+"F31.boolean.opBoolean","MERGE",FACE,{"derivedFrom":[makeQuery(id+"F5.boolean.opBoolean","MERGE",FACE,{"derivedFrom":[makeQuery(id+"F3.opExtrude","SWEPT_FACE",FACE,{"disambiguationData":[OSD([sQuery(id+"F2.wireOp",EDGE,"E4.left")])]}),makeQuery(id+"F5.opExtrude","SWEPT_FACE",FACE,{"disambiguationData":[OSD([sQuery(id+"F4.wireOp",EDGE,"E15")])]})]}),makeQuery(id+"F31.opExtrude","SWEPT_FACE",FACE,{"disambiguationData":[OSD([sQuery(id+"F30.wireOp",EDGE,"E93")])]})]});
            var sketch = newSketch(context, id + "F37", { "sketchPlane" : qUnion([Q0])});
            skCircle(sketch, "E97", {"center": v(18, 30.25) * mm, "radius": 3 * mm});
            skCircle(sketch, "E98", {"center": v(18, 10.25) * mm, "radius": 3 * mm});
            skLineSegment(sketch, "E99", {"start": v(28, 40) * mm, "end": v(28, 20.5) * mm});
            skLineSegment(sketch, "E100", {"start": v(28, 20.5) * mm, "end": v(28, 0) * mm});
            skPoint(sketch, "E101", {"position": v(28, 30.25) * mm});
            skPoint(sketch, "E102", {"position": v(28, 10.25) * mm});
            skSolve(sketch);
        }
        {
            var Q0;
            Q0 = qSketchRegion(id + "F37", true);
            extrude(context, id + "F38", {"entities" : qUnion([Q0]), "operationType" : NewBodyOperationType.REMOVE, "endBound" : BoundingType.THROUGH_ALL, "oppositeDirection" : true, "depth" : 25 * mm});
        }
        {
            var Q0;
            Q0=makeQuery(id+"F5.opExtrude","SWEPT_FACE",FACE,{"disambiguationData":[OSD([sQuery(id+"F4.wireOp",EDGE,"E18")])]});
            var sketch = newSketch(context, id + "F39", { "sketchPlane" : qUnion([Q0])});
            skCircle(sketch, "E103", {"center": v(18, 30.25) * mm, "radius": 5 * mm});
            skCircle(sketch, "E104", {"center": v(18, 10.25) * mm, "radius": 5 * mm});
            skSolve(sketch);
        }
        {
            var Q0;
            Q0 = qSketchRegion(id + "F39", true);
            extrude(context, id + "F40", {"entities" : qUnion([Q0]), "operationType" : NewBodyOperationType.REMOVE, "oppositeDirection" : true, "depth" : 3 * mm});
        }
        {
            var Q0;
            Q0=makeQuery(id+"F5.opExtrude","SWEPT_FACE",FACE,{"disambiguationData":[OSD([sQuery(id+"F4.wireOp",EDGE,"E17")])]});
            var sketch = newSketch(context, id + "F41", { "sketchPlane" : qUnion([Q0])});
            skCircle(sketch, "E105", {"center": v(-18, 10.25) * mm, "radius": 5 * mm});
            skCircle(sketch, "E106", {"center": v(-18, 30.25) * mm, "radius": 5 * mm});
            skSolve(sketch);
        }
        {
            var Q0;
            Q0 = qSketchRegion(id + "F41", true);
            extrude(context, id + "F42", {"entities" : qUnion([Q0]), "operationType" : NewBodyOperationType.REMOVE, "oppositeDirection" : true, "depth" : 3 * mm});
        }
    });
